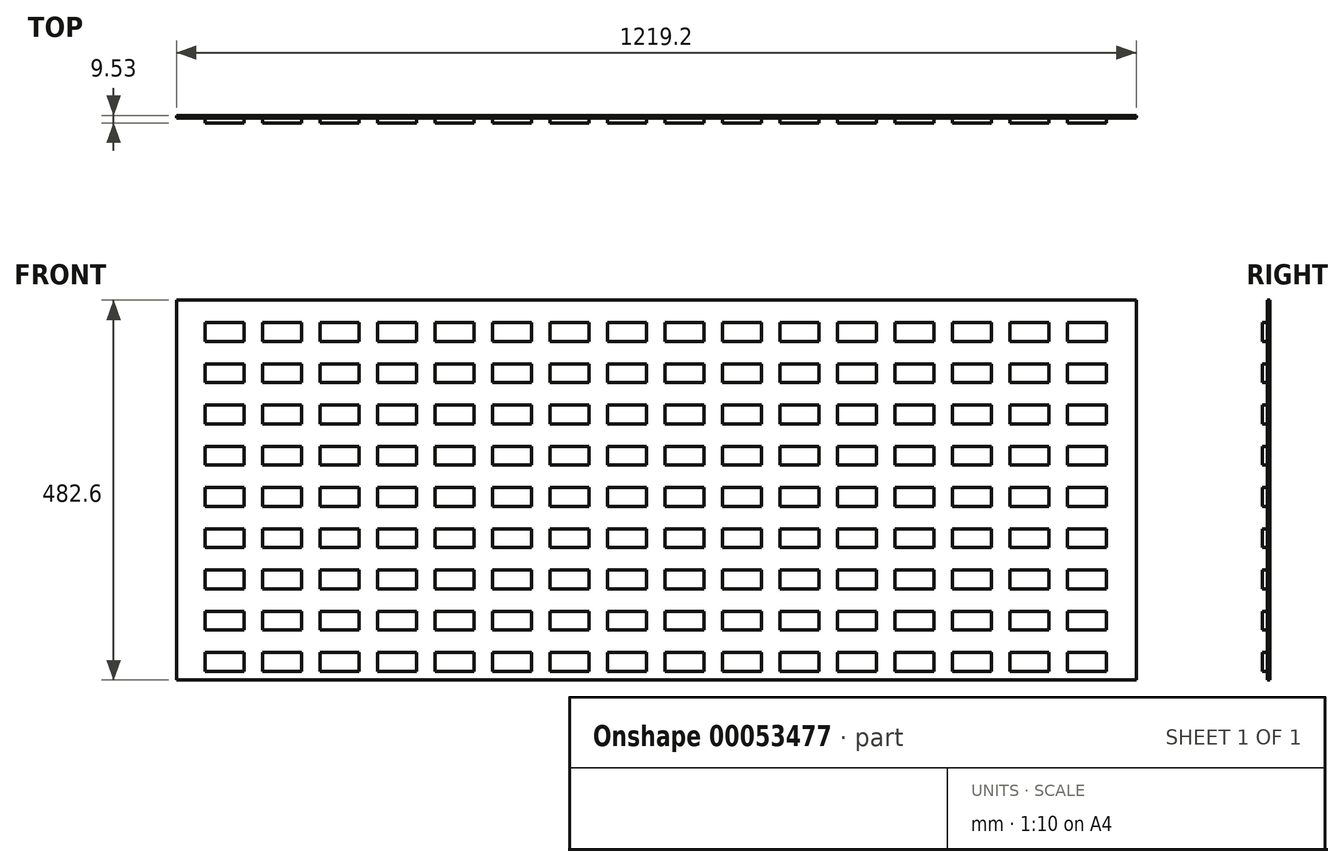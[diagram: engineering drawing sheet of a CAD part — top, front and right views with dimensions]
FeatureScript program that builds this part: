
annotation { "Feature Type Name" : "Feature", "Feature Type Description" : "" }
export const myFeature = defineFeature(function(context is Context, id is Id, definition is map)
    precondition{}
    {
        {
            var Q0;
            Q0=qCreatedBy(makeId("Front.planeOp"),FACE);
            var sketch = newSketch(context, id + "F0", { "sketchPlane" : qUnion([Q0])});
            skLineSegment(sketch, "E0.rect.bottom", {"start": v(-609.6, 241.3) * mm, "end": v(609.6, 241.3) * mm});
            skLineSegment(sketch, "E0.rect.top", {"start": v(-609.6, -241.3) * mm, "end": v(609.6, -241.3) * mm});
            skLineSegment(sketch, "E0.rect.left", {"start": v(-609.6, 241.3) * mm, "end": v(-609.6, -241.3) * mm});
            skLineSegment(sketch, "E0.rect.right", {"start": v(609.6, 241.3) * mm, "end": v(609.6, -241.3) * mm});
            skPoint(sketch, "E0.rect.middle", {"position": v(0, 0) * mm});
            skSolve(sketch);
        }
        {
            var Q0;
            Q0 = qSketchRegion(id + "F0", true);
            extrude(context, id + "F1", {"entities" : qUnion([Q0]), "depth" : 3.17 * mm});
        }
        {
            var Q0;
            Q0=makeQuery(id+"F1.opExtrude","CAP_FACE",FACE,{"disambiguationData":[OSD([sQuery(id+"F0.wireOp",EDGE,"E0.rect.bottom"),sQuery(id+"F0.wireOp",EDGE,"E0.rect.top"),sQuery(id+"F0.wireOp",EDGE,"E0.rect.left"),sQuery(id+"F0.wireOp",EDGE,"E0.rect.right")])],"isStart":false});
            var sketch = newSketch(context, id + "F2", { "sketchPlane" : qUnion([Q0])});
            skLineSegment(sketch, "E1", {"start": v(-609.6, 241.3) * mm, "end": v(-609.6, 212.72) * mm, "construction": true});
            skLineSegment(sketch, "E2", {"start": v(-609.6, 212.72) * mm, "end": v(-573.09, 212.72) * mm, "construction": true});
            skLineSegment(sketch, "E3", {"start": v(-573.09, 212.72) * mm, "end": v(-523.87, 212.72) * mm});
            skLineSegment(sketch, "E4", {"start": v(-523.87, 212.72) * mm, "end": v(-523.87, 188.91) * mm});
            skLineSegment(sketch, "E5", {"start": v(-523.87, 188.91) * mm, "end": v(-573.09, 188.91) * mm});
            skLineSegment(sketch, "E6", {"start": v(-573.09, 188.91) * mm, "end": v(-573.09, 212.72) * mm});
            skLineSegment(sketch, "E7", {"start": v(-548.48, 188.91) * mm, "end": v(-548.48, 160.34) * mm, "construction": true});
            skLineSegment(sketch, "E8.bottom", {"start": v(-573.09, 160.34) * mm, "end": v(-523.88, 160.34) * mm});
            skLineSegment(sketch, "E8.top", {"start": v(-573.09, 136.52) * mm, "end": v(-523.88, 136.52) * mm});
            skLineSegment(sketch, "E8.left", {"start": v(-573.09, 160.34) * mm, "end": v(-573.09, 136.52) * mm});
            skLineSegment(sketch, "E8.right", {"start": v(-523.88, 160.34) * mm, "end": v(-523.88, 136.52) * mm});
            skLineSegment(sketch, "E9", {"start": v(-523.87, 200.82) * mm, "end": v(-500.06, 200.82) * mm, "construction": true});
            skLineSegment(sketch, "E10", {"start": v(-500.06, 200.82) * mm, "end": v(-450.85, 200.82) * mm, "construction": true});
            skLineSegment(sketch, "E11", {"start": v(-450.85, 200.82) * mm, "end": v(-427.04, 200.82) * mm, "construction": true});
            skLineSegment(sketch, "E12", {"start": v(-427.04, 200.82) * mm, "end": v(-377.82, 200.82) * mm, "construction": true});
            skLineSegment(sketch, "E13", {"start": v(-377.82, 200.82) * mm, "end": v(-354.01, 200.82) * mm, "construction": true});
            skLineSegment(sketch, "E14", {"start": v(-354.01, 200.82) * mm, "end": v(-304.8, 200.82) * mm, "construction": true});
            skLineSegment(sketch, "E15", {"start": v(-304.8, 200.82) * mm, "end": v(-280.99, 200.82) * mm, "construction": true});
            skLineSegment(sketch, "E16", {"start": v(-280.99, 200.82) * mm, "end": v(-231.77, 200.82) * mm, "construction": true});
            skLineSegment(sketch, "E17", {"start": v(-231.77, 200.82) * mm, "end": v(-207.96, 200.82) * mm, "construction": true});
            skLineSegment(sketch, "E18", {"start": v(-207.96, 200.82) * mm, "end": v(-158.75, 200.82) * mm, "construction": true});
            skLineSegment(sketch, "E19", {"start": v(-158.75, 200.82) * mm, "end": v(-134.94, 200.82) * mm, "construction": true});
            skLineSegment(sketch, "E20", {"start": v(-134.94, 200.82) * mm, "end": v(-85.72, 200.82) * mm, "construction": true});
            skLineSegment(sketch, "E21", {"start": v(-85.72, 200.82) * mm, "end": v(-61.91, 200.82) * mm, "construction": true});
            skLineSegment(sketch, "E22", {"start": v(-61.91, 200.82) * mm, "end": v(-12.7, 200.82) * mm, "construction": true});
            skLineSegment(sketch, "E23", {"start": v(-12.7, 200.82) * mm, "end": v(11.11, 200.82) * mm, "construction": true});
            skLineSegment(sketch, "E24", {"start": v(11.11, 200.82) * mm, "end": v(60.33, 200.82) * mm, "construction": true});
            skLineSegment(sketch, "E25", {"start": v(60.33, 200.82) * mm, "end": v(84.14, 200.82) * mm, "construction": true});
            skLineSegment(sketch, "E26", {"start": v(84.14, 200.82) * mm, "end": v(133.35, 200.82) * mm, "construction": true});
            skLineSegment(sketch, "E27", {"start": v(133.35, 200.82) * mm, "end": v(157.16, 200.82) * mm, "construction": true});
            skLineSegment(sketch, "E28", {"start": v(157.16, 200.82) * mm, "end": v(206.38, 200.82) * mm, "construction": true});
            skLineSegment(sketch, "E29", {"start": v(206.38, 200.82) * mm, "end": v(230.19, 200.82) * mm, "construction": true});
            skLineSegment(sketch, "E30", {"start": v(230.19, 200.82) * mm, "end": v(279.4, 200.82) * mm, "construction": true});
            skLineSegment(sketch, "E31", {"start": v(279.4, 200.82) * mm, "end": v(303.21, 200.82) * mm, "construction": true});
            skLineSegment(sketch, "E32", {"start": v(303.21, 200.82) * mm, "end": v(352.43, 200.82) * mm, "construction": true});
            skLineSegment(sketch, "E33", {"start": v(352.43, 200.82) * mm, "end": v(376.24, 200.82) * mm, "construction": true});
            skLineSegment(sketch, "E34", {"start": v(376.24, 200.82) * mm, "end": v(425.45, 200.82) * mm, "construction": true});
            skLineSegment(sketch, "E35", {"start": v(425.45, 200.82) * mm, "end": v(449.26, 200.82) * mm, "construction": true});
            skLineSegment(sketch, "E36", {"start": v(449.26, 200.82) * mm, "end": v(498.48, 200.82) * mm, "construction": true});
            skLineSegment(sketch, "E37", {"start": v(498.48, 200.82) * mm, "end": v(522.29, 200.82) * mm, "construction": true});
            skLineSegment(sketch, "E38.rect.bottom", {"start": v(-450.85, 188.91) * mm, "end": v(-500.06, 188.91) * mm});
            skLineSegment(sketch, "E38.rect.top", {"start": v(-450.85, 212.73) * mm, "end": v(-500.06, 212.73) * mm});
            skLineSegment(sketch, "E38.rect.left", {"start": v(-450.85, 188.91) * mm, "end": v(-450.85, 212.73) * mm});
            skLineSegment(sketch, "E38.rect.right", {"start": v(-500.06, 188.91) * mm, "end": v(-500.06, 212.73) * mm});
            skPoint(sketch, "E38.rect.middle", {"position": v(-475.46, 200.82) * mm});
            skLineSegment(sketch, "E39.rect.bottom", {"start": v(-427.04, 188.91) * mm, "end": v(-377.82, 188.91) * mm});
            skLineSegment(sketch, "E39.rect.top", {"start": v(-427.04, 212.72) * mm, "end": v(-377.82, 212.72) * mm});
            skLineSegment(sketch, "E39.rect.left", {"start": v(-427.04, 188.91) * mm, "end": v(-427.04, 212.72) * mm});
            skLineSegment(sketch, "E39.rect.right", {"start": v(-377.82, 188.91) * mm, "end": v(-377.82, 212.72) * mm});
            skPoint(sketch, "E39.rect.middle", {"position": v(-402.43, 200.82) * mm});
            skLineSegment(sketch, "E40.rect.bottom", {"start": v(-354.01, 188.91) * mm, "end": v(-304.8, 188.91) * mm});
            skLineSegment(sketch, "E40.rect.top", {"start": v(-354.01, 212.73) * mm, "end": v(-304.8, 212.73) * mm});
            skLineSegment(sketch, "E40.rect.left", {"start": v(-354.01, 188.91) * mm, "end": v(-354.01, 212.73) * mm});
            skLineSegment(sketch, "E40.rect.right", {"start": v(-304.8, 188.91) * mm, "end": v(-304.8, 212.73) * mm});
            skPoint(sketch, "E40.rect.middle", {"position": v(-329.4, 200.82) * mm});
            skPoint(sketch, "E40.rect.cornerSnap0", {"position": v(-402.43, 188.91) * mm});
            skLineSegment(sketch, "E41.rect.bottom", {"start": v(-280.99, 188.91) * mm, "end": v(-231.77, 188.91) * mm});
            skLineSegment(sketch, "E41.rect.top", {"start": v(-280.99, 212.72) * mm, "end": v(-231.77, 212.72) * mm});
            skLineSegment(sketch, "E41.rect.left", {"start": v(-280.99, 188.91) * mm, "end": v(-280.99, 212.72) * mm});
            skLineSegment(sketch, "E41.rect.right", {"start": v(-231.77, 188.91) * mm, "end": v(-231.77, 212.72) * mm});
            skPoint(sketch, "E41.rect.middle", {"position": v(-256.38, 200.82) * mm});
            skLineSegment(sketch, "E42.rect.bottom", {"start": v(-207.96, 188.91) * mm, "end": v(-158.75, 188.91) * mm});
            skLineSegment(sketch, "E42.rect.top", {"start": v(-207.96, 212.72) * mm, "end": v(-158.75, 212.72) * mm});
            skLineSegment(sketch, "E42.rect.left", {"start": v(-207.96, 188.91) * mm, "end": v(-207.96, 212.72) * mm});
            skLineSegment(sketch, "E42.rect.right", {"start": v(-158.75, 188.91) * mm, "end": v(-158.75, 212.72) * mm});
            skPoint(sketch, "E42.rect.middle", {"position": v(-183.36, 200.82) * mm});
            skLineSegment(sketch, "E43.rect.bottom", {"start": v(-134.94, 188.91) * mm, "end": v(-85.72, 188.91) * mm});
            skLineSegment(sketch, "E43.rect.top", {"start": v(-134.94, 212.73) * mm, "end": v(-85.72, 212.73) * mm});
            skLineSegment(sketch, "E43.rect.left", {"start": v(-134.94, 188.91) * mm, "end": v(-134.94, 212.73) * mm});
            skLineSegment(sketch, "E43.rect.right", {"start": v(-85.72, 188.91) * mm, "end": v(-85.72, 212.73) * mm});
            skPoint(sketch, "E43.rect.middle", {"position": v(-110.33, 200.82) * mm});
            skLineSegment(sketch, "E44.rect.bottom", {"start": v(-61.91, 188.91) * mm, "end": v(-12.7, 188.91) * mm});
            skLineSegment(sketch, "E44.rect.top", {"start": v(-61.91, 212.73) * mm, "end": v(-12.7, 212.73) * mm});
            skLineSegment(sketch, "E44.rect.left", {"start": v(-61.91, 188.91) * mm, "end": v(-61.91, 212.73) * mm});
            skLineSegment(sketch, "E44.rect.right", {"start": v(-12.7, 188.91) * mm, "end": v(-12.7, 212.73) * mm});
            skPoint(sketch, "E44.rect.middle", {"position": v(-37.3, 200.82) * mm});
            skLineSegment(sketch, "E45.rect.bottom", {"start": v(11.11, 188.91) * mm, "end": v(60.33, 188.91) * mm});
            skLineSegment(sketch, "E45.rect.top", {"start": v(11.11, 212.73) * mm, "end": v(60.33, 212.73) * mm});
            skLineSegment(sketch, "E45.rect.left", {"start": v(11.11, 188.91) * mm, "end": v(11.11, 212.73) * mm});
            skLineSegment(sketch, "E45.rect.right", {"start": v(60.33, 188.91) * mm, "end": v(60.33, 212.73) * mm});
            skPoint(sketch, "E45.rect.middle", {"position": v(35.72, 200.82) * mm});
            skLineSegment(sketch, "E46.rect.bottom", {"start": v(84.14, 188.91) * mm, "end": v(133.35, 188.91) * mm});
            skLineSegment(sketch, "E46.rect.top", {"start": v(84.14, 212.72) * mm, "end": v(133.35, 212.72) * mm});
            skLineSegment(sketch, "E46.rect.left", {"start": v(84.14, 188.91) * mm, "end": v(84.14, 212.72) * mm});
            skLineSegment(sketch, "E46.rect.right", {"start": v(133.35, 188.91) * mm, "end": v(133.35, 212.72) * mm});
            skPoint(sketch, "E46.rect.middle", {"position": v(108.74, 200.82) * mm});
            skLineSegment(sketch, "E47.rect.bottom", {"start": v(157.16, 188.91) * mm, "end": v(206.38, 188.91) * mm});
            skLineSegment(sketch, "E47.rect.top", {"start": v(157.16, 212.72) * mm, "end": v(206.38, 212.72) * mm});
            skLineSegment(sketch, "E47.rect.left", {"start": v(157.16, 188.91) * mm, "end": v(157.16, 212.72) * mm});
            skLineSegment(sketch, "E47.rect.right", {"start": v(206.38, 188.91) * mm, "end": v(206.38, 212.72) * mm});
            skPoint(sketch, "E47.rect.middle", {"position": v(181.77, 200.82) * mm});
            skLineSegment(sketch, "E48.rect.bottom", {"start": v(230.19, 188.91) * mm, "end": v(279.4, 188.91) * mm});
            skLineSegment(sketch, "E48.rect.top", {"start": v(230.19, 212.72) * mm, "end": v(279.4, 212.72) * mm});
            skLineSegment(sketch, "E48.rect.left", {"start": v(230.19, 188.91) * mm, "end": v(230.19, 212.72) * mm});
            skLineSegment(sketch, "E48.rect.right", {"start": v(279.4, 188.91) * mm, "end": v(279.4, 212.72) * mm});
            skPoint(sketch, "E48.rect.middle", {"position": v(254.8, 200.82) * mm});
            skLineSegment(sketch, "E49.rect.bottom", {"start": v(303.21, 188.91) * mm, "end": v(352.43, 188.91) * mm});
            skLineSegment(sketch, "E49.rect.top", {"start": v(303.21, 212.73) * mm, "end": v(352.43, 212.73) * mm});
            skLineSegment(sketch, "E49.rect.left", {"start": v(303.21, 188.91) * mm, "end": v(303.21, 212.73) * mm});
            skLineSegment(sketch, "E49.rect.right", {"start": v(352.43, 188.91) * mm, "end": v(352.43, 212.73) * mm});
            skPoint(sketch, "E49.rect.middle", {"position": v(327.82, 200.82) * mm});
            skLineSegment(sketch, "E50.rect.bottom", {"start": v(376.24, 188.91) * mm, "end": v(425.45, 188.91) * mm});
            skLineSegment(sketch, "E50.rect.top", {"start": v(376.24, 212.73) * mm, "end": v(425.45, 212.73) * mm});
            skLineSegment(sketch, "E50.rect.left", {"start": v(376.24, 188.91) * mm, "end": v(376.24, 212.73) * mm});
            skLineSegment(sketch, "E50.rect.right", {"start": v(425.45, 188.91) * mm, "end": v(425.45, 212.73) * mm});
            skPoint(sketch, "E50.rect.middle", {"position": v(400.84, 200.82) * mm});
            skLineSegment(sketch, "E51.rect.bottom", {"start": v(449.26, 188.91) * mm, "end": v(498.48, 188.91) * mm});
            skLineSegment(sketch, "E51.rect.top", {"start": v(449.26, 212.73) * mm, "end": v(498.48, 212.73) * mm});
            skLineSegment(sketch, "E51.rect.left", {"start": v(449.26, 188.91) * mm, "end": v(449.26, 212.73) * mm});
            skLineSegment(sketch, "E51.rect.right", {"start": v(498.48, 188.91) * mm, "end": v(498.48, 212.73) * mm});
            skPoint(sketch, "E51.rect.middle", {"position": v(473.87, 200.82) * mm});
            skLineSegment(sketch, "E52", {"start": v(-523.88, 148.43) * mm, "end": v(-500.06, 148.43) * mm, "construction": true});
            skLineSegment(sketch, "E53", {"start": v(-500.06, 148.43) * mm, "end": v(-450.85, 148.43) * mm, "construction": true});
            skLineSegment(sketch, "E54", {"start": v(-450.85, 148.43) * mm, "end": v(-427.04, 148.43) * mm, "construction": true});
            skLineSegment(sketch, "E55", {"start": v(-427.04, 148.43) * mm, "end": v(-377.82, 148.43) * mm, "construction": true});
            skLineSegment(sketch, "E56", {"start": v(-377.82, 148.43) * mm, "end": v(-354.01, 148.43) * mm, "construction": true});
            skLineSegment(sketch, "E57", {"start": v(-354.01, 148.43) * mm, "end": v(-304.8, 148.43) * mm, "construction": true});
            skLineSegment(sketch, "E58", {"start": v(-304.8, 148.43) * mm, "end": v(-280.99, 148.43) * mm, "construction": true});
            skLineSegment(sketch, "E59", {"start": v(-280.99, 148.43) * mm, "end": v(-231.77, 148.43) * mm, "construction": true});
            skLineSegment(sketch, "E60", {"start": v(-231.77, 148.43) * mm, "end": v(-207.96, 148.43) * mm, "construction": true});
            skLineSegment(sketch, "E61", {"start": v(-207.96, 148.43) * mm, "end": v(-158.75, 148.43) * mm, "construction": true});
            skLineSegment(sketch, "E62.rect.bottom", {"start": v(-500.06, 160.34) * mm, "end": v(-450.85, 160.34) * mm});
            skLineSegment(sketch, "E62.rect.top", {"start": v(-500.06, 136.52) * mm, "end": v(-450.85, 136.52) * mm});
            skLineSegment(sketch, "E62.rect.left", {"start": v(-500.06, 160.34) * mm, "end": v(-500.06, 136.52) * mm});
            skLineSegment(sketch, "E62.rect.right", {"start": v(-450.85, 160.34) * mm, "end": v(-450.85, 136.52) * mm});
            skPoint(sketch, "E62.rect.middle", {"position": v(-475.46, 148.43) * mm});
            skLineSegment(sketch, "E63.rect.bottom", {"start": v(-427.04, 160.34) * mm, "end": v(-377.82, 160.34) * mm});
            skLineSegment(sketch, "E63.rect.top", {"start": v(-427.04, 136.53) * mm, "end": v(-377.82, 136.53) * mm});
            skLineSegment(sketch, "E63.rect.left", {"start": v(-427.04, 160.34) * mm, "end": v(-427.04, 136.53) * mm});
            skLineSegment(sketch, "E63.rect.right", {"start": v(-377.82, 160.34) * mm, "end": v(-377.82, 136.53) * mm});
            skPoint(sketch, "E63.rect.middle", {"position": v(-402.43, 148.43) * mm});
            skLineSegment(sketch, "E64.rect.bottom", {"start": v(-354.01, 160.34) * mm, "end": v(-304.8, 160.34) * mm});
            skLineSegment(sketch, "E64.rect.top", {"start": v(-354.01, 136.53) * mm, "end": v(-304.8, 136.53) * mm});
            skLineSegment(sketch, "E64.rect.left", {"start": v(-354.01, 160.34) * mm, "end": v(-354.01, 136.53) * mm});
            skLineSegment(sketch, "E64.rect.right", {"start": v(-304.8, 160.34) * mm, "end": v(-304.8, 136.53) * mm});
            skPoint(sketch, "E64.rect.middle", {"position": v(-329.4, 148.43) * mm});
            skLineSegment(sketch, "E65.rect.bottom", {"start": v(-280.99, 160.34) * mm, "end": v(-231.77, 160.34) * mm});
            skLineSegment(sketch, "E65.rect.top", {"start": v(-280.99, 136.52) * mm, "end": v(-231.77, 136.52) * mm});
            skLineSegment(sketch, "E65.rect.left", {"start": v(-280.99, 160.34) * mm, "end": v(-280.99, 136.52) * mm});
            skLineSegment(sketch, "E65.rect.right", {"start": v(-231.77, 160.34) * mm, "end": v(-231.77, 136.52) * mm});
            skPoint(sketch, "E65.rect.middle", {"position": v(-256.38, 148.43) * mm});
            skLineSegment(sketch, "E66.rect.bottom", {"start": v(-207.96, 160.34) * mm, "end": v(-158.75, 160.34) * mm});
            skLineSegment(sketch, "E66.rect.top", {"start": v(-207.96, 136.52) * mm, "end": v(-158.75, 136.52) * mm});
            skLineSegment(sketch, "E66.rect.left", {"start": v(-207.96, 160.34) * mm, "end": v(-207.96, 136.52) * mm});
            skLineSegment(sketch, "E66.rect.right", {"start": v(-158.75, 160.34) * mm, "end": v(-158.75, 136.52) * mm});
            skPoint(sketch, "E66.rect.middle", {"position": v(-183.36, 148.43) * mm});
            skLineSegment(sketch, "E67", {"start": v(-158.75, 148.43) * mm, "end": v(-134.94, 148.43) * mm, "construction": true});
            skLineSegment(sketch, "E68", {"start": v(-134.94, 148.43) * mm, "end": v(-85.72, 148.43) * mm, "construction": true});
            skLineSegment(sketch, "E69", {"start": v(-85.72, 148.43) * mm, "end": v(-61.91, 148.43) * mm, "construction": true});
            skLineSegment(sketch, "E70", {"start": v(-61.91, 148.43) * mm, "end": v(-12.7, 148.43) * mm, "construction": true});
            skLineSegment(sketch, "E71", {"start": v(-12.7, 148.43) * mm, "end": v(11.11, 148.43) * mm, "construction": true});
            skLineSegment(sketch, "E72", {"start": v(11.11, 148.43) * mm, "end": v(60.33, 148.43) * mm, "construction": true});
            skLineSegment(sketch, "E73", {"start": v(60.33, 148.43) * mm, "end": v(84.14, 148.43) * mm, "construction": true});
            skLineSegment(sketch, "E74", {"start": v(84.14, 148.43) * mm, "end": v(133.35, 148.43) * mm, "construction": true});
            skLineSegment(sketch, "E75", {"start": v(133.35, 148.43) * mm, "end": v(157.16, 148.43) * mm, "construction": true});
            skLineSegment(sketch, "E76", {"start": v(157.16, 148.43) * mm, "end": v(206.38, 148.43) * mm, "construction": true});
            skLineSegment(sketch, "E77.rect.bottom", {"start": v(-134.94, 160.34) * mm, "end": v(-85.72, 160.34) * mm});
            skLineSegment(sketch, "E77.rect.top", {"start": v(-134.94, 136.52) * mm, "end": v(-85.72, 136.52) * mm});
            skLineSegment(sketch, "E77.rect.left", {"start": v(-134.94, 160.34) * mm, "end": v(-134.94, 136.52) * mm});
            skLineSegment(sketch, "E77.rect.right", {"start": v(-85.72, 160.34) * mm, "end": v(-85.72, 136.52) * mm});
            skPoint(sketch, "E77.rect.middle", {"position": v(-110.33, 148.43) * mm});
            skLineSegment(sketch, "E78.rect.bottom", {"start": v(-61.91, 160.34) * mm, "end": v(-12.7, 160.34) * mm});
            skLineSegment(sketch, "E78.rect.top", {"start": v(-61.91, 136.52) * mm, "end": v(-12.7, 136.52) * mm});
            skLineSegment(sketch, "E78.rect.left", {"start": v(-61.91, 160.34) * mm, "end": v(-61.91, 136.52) * mm});
            skLineSegment(sketch, "E78.rect.right", {"start": v(-12.7, 160.34) * mm, "end": v(-12.7, 136.52) * mm});
            skPoint(sketch, "E78.rect.middle", {"position": v(-37.3, 148.43) * mm});
            skLineSegment(sketch, "E79.rect.bottom", {"start": v(11.11, 160.34) * mm, "end": v(60.33, 160.34) * mm});
            skLineSegment(sketch, "E79.rect.top", {"start": v(11.11, 136.52) * mm, "end": v(60.33, 136.52) * mm});
            skLineSegment(sketch, "E79.rect.left", {"start": v(11.11, 160.34) * mm, "end": v(11.11, 136.52) * mm});
            skLineSegment(sketch, "E79.rect.right", {"start": v(60.33, 160.34) * mm, "end": v(60.33, 136.52) * mm});
            skPoint(sketch, "E79.rect.middle", {"position": v(35.72, 148.43) * mm});
            skLineSegment(sketch, "E80.rect.bottom", {"start": v(84.14, 160.34) * mm, "end": v(133.35, 160.34) * mm});
            skLineSegment(sketch, "E80.rect.top", {"start": v(84.14, 136.52) * mm, "end": v(133.35, 136.52) * mm});
            skLineSegment(sketch, "E80.rect.left", {"start": v(84.14, 160.34) * mm, "end": v(84.14, 136.52) * mm});
            skLineSegment(sketch, "E80.rect.right", {"start": v(133.35, 160.34) * mm, "end": v(133.35, 136.52) * mm});
            skPoint(sketch, "E80.rect.middle", {"position": v(108.74, 148.43) * mm});
            skLineSegment(sketch, "E81.rect.bottom", {"start": v(157.16, 160.34) * mm, "end": v(206.38, 160.34) * mm});
            skLineSegment(sketch, "E81.rect.top", {"start": v(157.16, 136.52) * mm, "end": v(206.38, 136.52) * mm});
            skLineSegment(sketch, "E81.rect.left", {"start": v(157.16, 160.34) * mm, "end": v(157.16, 136.52) * mm});
            skLineSegment(sketch, "E81.rect.right", {"start": v(206.38, 160.34) * mm, "end": v(206.38, 136.52) * mm});
            skPoint(sketch, "E81.rect.middle", {"position": v(181.77, 148.43) * mm});
            skLineSegment(sketch, "E82", {"start": v(206.38, 148.43) * mm, "end": v(230.19, 148.43) * mm, "construction": true});
            skLineSegment(sketch, "E83", {"start": v(230.19, 148.43) * mm, "end": v(279.4, 148.43) * mm, "construction": true});
            skLineSegment(sketch, "E84", {"start": v(279.4, 148.43) * mm, "end": v(303.21, 148.43) * mm, "construction": true});
            skLineSegment(sketch, "E85", {"start": v(303.21, 148.43) * mm, "end": v(352.43, 148.43) * mm, "construction": true});
            skLineSegment(sketch, "E86", {"start": v(352.43, 148.43) * mm, "end": v(376.24, 148.43) * mm, "construction": true});
            skLineSegment(sketch, "E87", {"start": v(376.24, 148.43) * mm, "end": v(425.45, 148.43) * mm, "construction": true});
            skLineSegment(sketch, "E88", {"start": v(425.45, 148.43) * mm, "end": v(449.26, 148.43) * mm, "construction": true});
            skLineSegment(sketch, "E89", {"start": v(449.26, 148.43) * mm, "end": v(498.48, 148.43) * mm, "construction": true});
            skLineSegment(sketch, "E90.rect.bottom", {"start": v(230.19, 160.34) * mm, "end": v(279.4, 160.34) * mm});
            skLineSegment(sketch, "E90.rect.top", {"start": v(230.19, 136.52) * mm, "end": v(279.4, 136.52) * mm});
            skLineSegment(sketch, "E90.rect.left", {"start": v(230.19, 160.34) * mm, "end": v(230.19, 136.52) * mm});
            skLineSegment(sketch, "E90.rect.right", {"start": v(279.4, 160.34) * mm, "end": v(279.4, 136.52) * mm});
            skPoint(sketch, "E90.rect.middle", {"position": v(254.8, 148.43) * mm});
            skLineSegment(sketch, "E91.rect.bottom", {"start": v(303.21, 160.34) * mm, "end": v(352.43, 160.34) * mm});
            skLineSegment(sketch, "E91.rect.top", {"start": v(303.21, 136.52) * mm, "end": v(352.43, 136.52) * mm});
            skLineSegment(sketch, "E91.rect.left", {"start": v(303.21, 160.34) * mm, "end": v(303.21, 136.52) * mm});
            skLineSegment(sketch, "E91.rect.right", {"start": v(352.43, 160.34) * mm, "end": v(352.43, 136.52) * mm});
            skPoint(sketch, "E91.rect.middle", {"position": v(327.82, 148.43) * mm});
            skLineSegment(sketch, "E92.rect.bottom", {"start": v(376.24, 160.34) * mm, "end": v(425.45, 160.34) * mm});
            skLineSegment(sketch, "E92.rect.top", {"start": v(376.24, 136.52) * mm, "end": v(425.45, 136.52) * mm});
            skLineSegment(sketch, "E92.rect.left", {"start": v(376.24, 160.34) * mm, "end": v(376.24, 136.52) * mm});
            skLineSegment(sketch, "E92.rect.right", {"start": v(425.45, 160.34) * mm, "end": v(425.45, 136.52) * mm});
            skPoint(sketch, "E92.rect.middle", {"position": v(400.84, 148.43) * mm});
            skLineSegment(sketch, "E93.rect.bottom", {"start": v(449.26, 160.34) * mm, "end": v(498.48, 160.34) * mm});
            skLineSegment(sketch, "E93.rect.top", {"start": v(449.26, 136.52) * mm, "end": v(498.48, 136.52) * mm});
            skLineSegment(sketch, "E93.rect.left", {"start": v(449.26, 160.34) * mm, "end": v(449.26, 136.52) * mm});
            skLineSegment(sketch, "E93.rect.right", {"start": v(498.48, 160.34) * mm, "end": v(498.48, 136.52) * mm});
            skPoint(sketch, "E93.rect.middle", {"position": v(473.87, 148.43) * mm});
            skLineSegment(sketch, "E94", {"start": v(522.29, 200.82) * mm, "end": v(571.5, 200.82) * mm, "construction": true});
            skLineSegment(sketch, "E95", {"start": v(571.5, 200.82) * mm, "end": v(608.01, 200.82) * mm, "construction": true});
            skLineSegment(sketch, "E96.rect.bottom", {"start": v(522.29, 212.73) * mm, "end": v(571.5, 212.73) * mm});
            skLineSegment(sketch, "E96.rect.top", {"start": v(522.29, 188.91) * mm, "end": v(571.5, 188.91) * mm});
            skLineSegment(sketch, "E96.rect.left", {"start": v(522.29, 212.73) * mm, "end": v(522.29, 188.91) * mm});
            skLineSegment(sketch, "E96.rect.right", {"start": v(571.5, 212.73) * mm, "end": v(571.5, 188.91) * mm});
            skPoint(sketch, "E96.rect.middle", {"position": v(546.9, 200.82) * mm});
            skLineSegment(sketch, "E97", {"start": v(498.48, 148.43) * mm, "end": v(522.29, 148.43) * mm, "construction": true});
            skLineSegment(sketch, "E98", {"start": v(522.29, 148.43) * mm, "end": v(571.5, 148.43) * mm, "construction": true});
            skLineSegment(sketch, "E99.rect.bottom", {"start": v(522.29, 160.34) * mm, "end": v(571.5, 160.34) * mm});
            skLineSegment(sketch, "E99.rect.top", {"start": v(522.29, 136.52) * mm, "end": v(571.5, 136.52) * mm});
            skLineSegment(sketch, "E99.rect.left", {"start": v(522.29, 160.34) * mm, "end": v(522.29, 136.52) * mm});
            skLineSegment(sketch, "E99.rect.right", {"start": v(571.5, 160.34) * mm, "end": v(571.5, 136.52) * mm});
            skPoint(sketch, "E99.rect.middle", {"position": v(546.9, 148.43) * mm});
            skSolve(sketch);
        }
        {
            var Q0;
            Q0 = qSketchRegion(id + "F2", true);
            extrude(context, id + "F3", {"entities" : qUnion([Q0]), "operationType" : NewBodyOperationType.ADD, "depth" : 6.35 * mm});
        }
        {
            var Q0;
            Q0=makeQuery(id+"F1.opExtrude","CAP_FACE",FACE,{"disambiguationData":[OSD([sQuery(id+"F0.wireOp",EDGE,"E0.rect.bottom"),sQuery(id+"F0.wireOp",EDGE,"E0.rect.top"),sQuery(id+"F0.wireOp",EDGE,"E0.rect.left"),sQuery(id+"F0.wireOp",EDGE,"E0.rect.right")])],"isStart":false});
            var sketch = newSketch(context, id + "F4", { "sketchPlane" : qUnion([Q0])});
            skLineSegment(sketch, "E100", {"start": v(-548.48, 136.52) * mm, "end": v(-548.48, 107.95) * mm, "construction": true});
            skLineSegment(sketch, "E101", {"start": v(-548.48, 107.95) * mm, "end": v(-548.48, 84.14) * mm, "construction": true});
            skLineSegment(sketch, "E102", {"start": v(-548.48, 84.14) * mm, "end": v(-548.48, 55.56) * mm, "construction": true});
            skLineSegment(sketch, "E103", {"start": v(-548.48, 55.56) * mm, "end": v(-548.48, 31.75) * mm, "construction": true});
            skLineSegment(sketch, "E104.rect.bottom", {"start": v(-573.09, 107.95) * mm, "end": v(-523.88, 107.95) * mm});
            skLineSegment(sketch, "E104.rect.top", {"start": v(-573.09, 84.14) * mm, "end": v(-523.88, 84.14) * mm});
            skLineSegment(sketch, "E104.rect.left", {"start": v(-573.09, 107.95) * mm, "end": v(-573.09, 84.14) * mm});
            skLineSegment(sketch, "E104.rect.right", {"start": v(-523.88, 107.95) * mm, "end": v(-523.88, 84.14) * mm});
            skPoint(sketch, "E104.rect.middle", {"position": v(-548.48, 96.04) * mm});
            skLineSegment(sketch, "E105.rect.bottom", {"start": v(-573.09, 55.56) * mm, "end": v(-523.88, 55.56) * mm});
            skLineSegment(sketch, "E105.rect.top", {"start": v(-573.09, 31.75) * mm, "end": v(-523.88, 31.75) * mm});
            skLineSegment(sketch, "E105.rect.left", {"start": v(-573.09, 55.56) * mm, "end": v(-573.09, 31.75) * mm});
            skLineSegment(sketch, "E105.rect.right", {"start": v(-523.88, 55.56) * mm, "end": v(-523.88, 31.75) * mm});
            skPoint(sketch, "E105.rect.middle", {"position": v(-548.48, 43.66) * mm});
            skLineSegment(sketch, "E106", {"start": v(-548.48, 31.75) * mm, "end": v(-548.48, 3.17) * mm, "construction": true});
            skLineSegment(sketch, "E107", {"start": v(-548.48, 3.17) * mm, "end": v(-548.48, -20.64) * mm, "construction": true});
            skLineSegment(sketch, "E108.rect.bottom", {"start": v(-573.09, 3.17) * mm, "end": v(-523.88, 3.17) * mm});
            skLineSegment(sketch, "E108.rect.top", {"start": v(-573.09, -20.64) * mm, "end": v(-523.88, -20.64) * mm});
            skLineSegment(sketch, "E108.rect.left", {"start": v(-573.09, 3.17) * mm, "end": v(-573.09, -20.64) * mm});
            skLineSegment(sketch, "E108.rect.right", {"start": v(-523.88, 3.17) * mm, "end": v(-523.88, -20.64) * mm});
            skPoint(sketch, "E108.rect.middle", {"position": v(-548.48, -8.73) * mm});
            skLineSegment(sketch, "E109", {"start": v(-523.88, 96.04) * mm, "end": v(-500.06, 96.04) * mm, "construction": true});
            skLineSegment(sketch, "E110", {"start": v(-500.06, 96.04) * mm, "end": v(-450.85, 96.04) * mm, "construction": true});
            skLineSegment(sketch, "E111", {"start": v(-450.85, 96.04) * mm, "end": v(-427.04, 96.04) * mm, "construction": true});
            skLineSegment(sketch, "E112", {"start": v(-427.04, 96.04) * mm, "end": v(-377.82, 96.04) * mm, "construction": true});
            skLineSegment(sketch, "E113", {"start": v(-377.82, 96.04) * mm, "end": v(-354.01, 96.04) * mm, "construction": true});
            skLineSegment(sketch, "E114", {"start": v(-354.01, 96.04) * mm, "end": v(-304.8, 96.04) * mm, "construction": true});
            skLineSegment(sketch, "E115", {"start": v(-304.8, 96.04) * mm, "end": v(-280.99, 96.04) * mm, "construction": true});
            skLineSegment(sketch, "E116", {"start": v(-280.99, 96.04) * mm, "end": v(-231.77, 96.04) * mm, "construction": true});
            skLineSegment(sketch, "E117", {"start": v(-231.77, 96.04) * mm, "end": v(-207.96, 96.04) * mm, "construction": true});
            skLineSegment(sketch, "E118", {"start": v(-207.96, 96.04) * mm, "end": v(-158.75, 96.04) * mm, "construction": true});
            skLineSegment(sketch, "E119", {"start": v(-158.75, 96.04) * mm, "end": v(-134.94, 96.04) * mm, "construction": true});
            skLineSegment(sketch, "E120", {"start": v(-523.88, 43.66) * mm, "end": v(-500.06, 43.66) * mm, "construction": true});
            skLineSegment(sketch, "E121", {"start": v(-500.06, 43.66) * mm, "end": v(-450.85, 43.66) * mm, "construction": true});
            skLineSegment(sketch, "E122", {"start": v(-450.85, 43.66) * mm, "end": v(-427.04, 43.66) * mm, "construction": true});
            skLineSegment(sketch, "E123", {"start": v(-427.04, 43.66) * mm, "end": v(-377.82, 43.66) * mm, "construction": true});
            skLineSegment(sketch, "E124", {"start": v(-377.82, 43.66) * mm, "end": v(-354.01, 43.66) * mm, "construction": true});
            skLineSegment(sketch, "E125", {"start": v(-354.01, 43.66) * mm, "end": v(-304.8, 43.66) * mm, "construction": true});
            skLineSegment(sketch, "E126", {"start": v(-304.8, 43.66) * mm, "end": v(-280.99, 43.66) * mm, "construction": true});
            skLineSegment(sketch, "E127", {"start": v(-280.99, 43.66) * mm, "end": v(-231.77, 43.66) * mm, "construction": true});
            skLineSegment(sketch, "E128", {"start": v(-231.77, 43.66) * mm, "end": v(-207.96, 43.66) * mm, "construction": true});
            skLineSegment(sketch, "E129", {"start": v(-207.96, 43.66) * mm, "end": v(-158.75, 43.66) * mm, "construction": true});
            skLineSegment(sketch, "E130", {"start": v(-158.75, 43.66) * mm, "end": v(-134.94, 43.66) * mm, "construction": true});
            skLineSegment(sketch, "E131", {"start": v(-523.88, -8.73) * mm, "end": v(-500.06, -8.73) * mm, "construction": true});
            skLineSegment(sketch, "E132", {"start": v(-500.06, -8.73) * mm, "end": v(-450.85, -8.73) * mm, "construction": true});
            skLineSegment(sketch, "E133", {"start": v(-450.85, -8.73) * mm, "end": v(-427.04, -8.73) * mm, "construction": true});
            skLineSegment(sketch, "E134", {"start": v(-427.04, -8.73) * mm, "end": v(-377.82, -8.73) * mm, "construction": true});
            skLineSegment(sketch, "E135", {"start": v(-377.82, -8.73) * mm, "end": v(-354.01, -8.73) * mm, "construction": true});
            skLineSegment(sketch, "E136", {"start": v(-354.01, -8.73) * mm, "end": v(-304.8, -8.73) * mm, "construction": true});
            skLineSegment(sketch, "E137", {"start": v(-304.8, -8.73) * mm, "end": v(-280.99, -8.73) * mm, "construction": true});
            skLineSegment(sketch, "E138", {"start": v(-280.99, -8.73) * mm, "end": v(-231.77, -8.73) * mm, "construction": true});
            skLineSegment(sketch, "E139", {"start": v(-231.77, -8.73) * mm, "end": v(-207.96, -8.73) * mm, "construction": true});
            skLineSegment(sketch, "E140", {"start": v(-207.96, -8.73) * mm, "end": v(-158.75, -8.73) * mm, "construction": true});
            skLineSegment(sketch, "E141", {"start": v(-158.75, -8.73) * mm, "end": v(-134.94, -8.73) * mm, "construction": true});
            skLineSegment(sketch, "E142.rect.bottom", {"start": v(-500.06, 107.95) * mm, "end": v(-450.85, 107.95) * mm});
            skLineSegment(sketch, "E142.rect.top", {"start": v(-500.06, 84.14) * mm, "end": v(-450.85, 84.14) * mm});
            skLineSegment(sketch, "E142.rect.left", {"start": v(-500.06, 107.95) * mm, "end": v(-500.06, 84.14) * mm});
            skLineSegment(sketch, "E142.rect.right", {"start": v(-450.85, 107.95) * mm, "end": v(-450.85, 84.14) * mm});
            skPoint(sketch, "E142.rect.middle", {"position": v(-475.46, 96.04) * mm});
            skLineSegment(sketch, "E143.rect.bottom", {"start": v(-427.04, 107.95) * mm, "end": v(-377.82, 107.95) * mm});
            skLineSegment(sketch, "E143.rect.top", {"start": v(-427.04, 84.14) * mm, "end": v(-377.82, 84.14) * mm});
            skLineSegment(sketch, "E143.rect.left", {"start": v(-427.04, 107.95) * mm, "end": v(-427.04, 84.14) * mm});
            skLineSegment(sketch, "E143.rect.right", {"start": v(-377.82, 107.95) * mm, "end": v(-377.82, 84.14) * mm});
            skPoint(sketch, "E143.rect.middle", {"position": v(-402.43, 96.04) * mm});
            skLineSegment(sketch, "E144.rect.bottom", {"start": v(-354.01, 107.95) * mm, "end": v(-304.8, 107.95) * mm});
            skLineSegment(sketch, "E144.rect.top", {"start": v(-354.01, 84.14) * mm, "end": v(-304.8, 84.14) * mm});
            skLineSegment(sketch, "E144.rect.left", {"start": v(-354.01, 107.95) * mm, "end": v(-354.01, 84.14) * mm});
            skLineSegment(sketch, "E144.rect.right", {"start": v(-304.8, 107.95) * mm, "end": v(-304.8, 84.14) * mm});
            skPoint(sketch, "E144.rect.middle", {"position": v(-329.4, 96.04) * mm});
            skLineSegment(sketch, "E145.rect.bottom", {"start": v(-280.99, 107.95) * mm, "end": v(-231.77, 107.95) * mm});
            skLineSegment(sketch, "E145.rect.top", {"start": v(-280.99, 84.14) * mm, "end": v(-231.77, 84.14) * mm});
            skLineSegment(sketch, "E145.rect.left", {"start": v(-280.99, 107.95) * mm, "end": v(-280.99, 84.14) * mm});
            skLineSegment(sketch, "E145.rect.right", {"start": v(-231.77, 107.95) * mm, "end": v(-231.77, 84.14) * mm});
            skPoint(sketch, "E145.rect.middle", {"position": v(-256.38, 96.04) * mm});
            skLineSegment(sketch, "E146.rect.bottom", {"start": v(-207.96, 107.95) * mm, "end": v(-158.75, 107.95) * mm});
            skLineSegment(sketch, "E146.rect.top", {"start": v(-207.96, 84.14) * mm, "end": v(-158.75, 84.14) * mm});
            skLineSegment(sketch, "E146.rect.left", {"start": v(-207.96, 107.95) * mm, "end": v(-207.96, 84.14) * mm});
            skLineSegment(sketch, "E146.rect.right", {"start": v(-158.75, 107.95) * mm, "end": v(-158.75, 84.14) * mm});
            skPoint(sketch, "E146.rect.middle", {"position": v(-183.36, 96.04) * mm});
            skLineSegment(sketch, "E147.rect.bottom", {"start": v(-500.06, 55.56) * mm, "end": v(-450.85, 55.56) * mm});
            skLineSegment(sketch, "E147.rect.top", {"start": v(-500.06, 31.75) * mm, "end": v(-450.85, 31.75) * mm});
            skLineSegment(sketch, "E147.rect.left", {"start": v(-500.06, 55.56) * mm, "end": v(-500.06, 31.75) * mm});
            skLineSegment(sketch, "E147.rect.right", {"start": v(-450.85, 55.56) * mm, "end": v(-450.85, 31.75) * mm});
            skPoint(sketch, "E147.rect.middle", {"position": v(-475.46, 43.66) * mm});
            skLineSegment(sketch, "E148.rect.bottom", {"start": v(-427.04, 55.56) * mm, "end": v(-377.82, 55.56) * mm});
            skLineSegment(sketch, "E148.rect.top", {"start": v(-427.04, 31.75) * mm, "end": v(-377.82, 31.75) * mm});
            skLineSegment(sketch, "E148.rect.left", {"start": v(-427.04, 55.56) * mm, "end": v(-427.04, 31.75) * mm});
            skLineSegment(sketch, "E148.rect.right", {"start": v(-377.82, 55.56) * mm, "end": v(-377.82, 31.75) * mm});
            skPoint(sketch, "E148.rect.middle", {"position": v(-402.43, 43.66) * mm});
            skLineSegment(sketch, "E149.rect.bottom", {"start": v(-354.01, 55.56) * mm, "end": v(-304.8, 55.56) * mm});
            skLineSegment(sketch, "E149.rect.top", {"start": v(-354.01, 31.75) * mm, "end": v(-304.8, 31.75) * mm});
            skLineSegment(sketch, "E149.rect.left", {"start": v(-354.01, 55.56) * mm, "end": v(-354.01, 31.75) * mm});
            skLineSegment(sketch, "E149.rect.right", {"start": v(-304.8, 55.56) * mm, "end": v(-304.8, 31.75) * mm});
            skPoint(sketch, "E149.rect.middle", {"position": v(-329.4, 43.66) * mm});
            skLineSegment(sketch, "E150.rect.bottom", {"start": v(-280.99, 55.56) * mm, "end": v(-231.77, 55.56) * mm});
            skLineSegment(sketch, "E150.rect.top", {"start": v(-280.99, 31.75) * mm, "end": v(-231.77, 31.75) * mm});
            skLineSegment(sketch, "E150.rect.left", {"start": v(-280.99, 55.56) * mm, "end": v(-280.99, 31.75) * mm});
            skLineSegment(sketch, "E150.rect.right", {"start": v(-231.77, 55.56) * mm, "end": v(-231.77, 31.75) * mm});
            skPoint(sketch, "E150.rect.middle", {"position": v(-256.38, 43.66) * mm});
            skLineSegment(sketch, "E151.rect.bottom", {"start": v(-207.96, 55.56) * mm, "end": v(-158.75, 55.56) * mm});
            skLineSegment(sketch, "E151.rect.top", {"start": v(-207.96, 31.75) * mm, "end": v(-158.75, 31.75) * mm});
            skLineSegment(sketch, "E151.rect.left", {"start": v(-207.96, 55.56) * mm, "end": v(-207.96, 31.75) * mm});
            skLineSegment(sketch, "E151.rect.right", {"start": v(-158.75, 55.56) * mm, "end": v(-158.75, 31.75) * mm});
            skPoint(sketch, "E151.rect.middle", {"position": v(-183.36, 43.66) * mm});
            skLineSegment(sketch, "E152.rect.bottom", {"start": v(-500.06, 3.17) * mm, "end": v(-450.85, 3.17) * mm});
            skLineSegment(sketch, "E152.rect.top", {"start": v(-500.06, -20.64) * mm, "end": v(-450.85, -20.64) * mm});
            skLineSegment(sketch, "E152.rect.left", {"start": v(-500.06, 3.17) * mm, "end": v(-500.06, -20.64) * mm});
            skLineSegment(sketch, "E152.rect.right", {"start": v(-450.85, 3.17) * mm, "end": v(-450.85, -20.64) * mm});
            skPoint(sketch, "E152.rect.middle", {"position": v(-475.46, -8.73) * mm});
            skLineSegment(sketch, "E153.rect.bottom", {"start": v(-427.04, 3.17) * mm, "end": v(-377.82, 3.17) * mm});
            skLineSegment(sketch, "E153.rect.top", {"start": v(-427.04, -20.64) * mm, "end": v(-377.82, -20.64) * mm});
            skLineSegment(sketch, "E153.rect.left", {"start": v(-427.04, 3.17) * mm, "end": v(-427.04, -20.64) * mm});
            skLineSegment(sketch, "E153.rect.right", {"start": v(-377.82, 3.17) * mm, "end": v(-377.82, -20.64) * mm});
            skPoint(sketch, "E153.rect.middle", {"position": v(-402.43, -8.73) * mm});
            skLineSegment(sketch, "E154.rect.bottom", {"start": v(-354.01, 3.17) * mm, "end": v(-304.8, 3.17) * mm});
            skLineSegment(sketch, "E154.rect.top", {"start": v(-354.01, -20.64) * mm, "end": v(-304.8, -20.64) * mm});
            skLineSegment(sketch, "E154.rect.left", {"start": v(-354.01, 3.17) * mm, "end": v(-354.01, -20.64) * mm});
            skLineSegment(sketch, "E154.rect.right", {"start": v(-304.8, 3.17) * mm, "end": v(-304.8, -20.64) * mm});
            skPoint(sketch, "E154.rect.middle", {"position": v(-329.4, -8.73) * mm});
            skLineSegment(sketch, "E155.rect.bottom", {"start": v(-280.99, 3.17) * mm, "end": v(-231.77, 3.17) * mm});
            skLineSegment(sketch, "E155.rect.top", {"start": v(-280.99, -20.64) * mm, "end": v(-231.77, -20.64) * mm});
            skLineSegment(sketch, "E155.rect.left", {"start": v(-280.99, 3.17) * mm, "end": v(-280.99, -20.64) * mm});
            skLineSegment(sketch, "E155.rect.right", {"start": v(-231.77, 3.17) * mm, "end": v(-231.77, -20.64) * mm});
            skPoint(sketch, "E155.rect.middle", {"position": v(-256.38, -8.73) * mm});
            skLineSegment(sketch, "E156.rect.bottom", {"start": v(-207.96, 3.17) * mm, "end": v(-158.75, 3.17) * mm});
            skLineSegment(sketch, "E156.rect.top", {"start": v(-207.96, -20.64) * mm, "end": v(-158.75, -20.64) * mm});
            skLineSegment(sketch, "E156.rect.left", {"start": v(-207.96, 3.17) * mm, "end": v(-207.96, -20.64) * mm});
            skLineSegment(sketch, "E156.rect.right", {"start": v(-158.75, 3.17) * mm, "end": v(-158.75, -20.64) * mm});
            skPoint(sketch, "E156.rect.middle", {"position": v(-183.36, -8.73) * mm});
            skLineSegment(sketch, "E157", {"start": v(-134.94, 96.04) * mm, "end": v(-85.72, 96.04) * mm, "construction": true});
            skLineSegment(sketch, "E158", {"start": v(-85.72, 96.04) * mm, "end": v(-61.91, 96.04) * mm, "construction": true});
            skLineSegment(sketch, "E159", {"start": v(-61.91, 96.04) * mm, "end": v(-12.7, 96.04) * mm, "construction": true});
            skLineSegment(sketch, "E160", {"start": v(-12.7, 96.04) * mm, "end": v(11.11, 96.04) * mm, "construction": true});
            skLineSegment(sketch, "E161", {"start": v(11.11, 96.04) * mm, "end": v(60.33, 96.04) * mm, "construction": true});
            skLineSegment(sketch, "E162", {"start": v(60.33, 96.04) * mm, "end": v(84.14, 96.04) * mm, "construction": true});
            skLineSegment(sketch, "E163", {"start": v(84.14, 96.04) * mm, "end": v(133.35, 96.04) * mm, "construction": true});
            skLineSegment(sketch, "E164", {"start": v(133.35, 96.04) * mm, "end": v(157.16, 96.04) * mm, "construction": true});
            skLineSegment(sketch, "E165", {"start": v(157.16, 96.04) * mm, "end": v(206.38, 96.04) * mm, "construction": true});
            skLineSegment(sketch, "E166", {"start": v(206.38, 96.04) * mm, "end": v(230.19, 96.04) * mm, "construction": true});
            skLineSegment(sketch, "E167", {"start": v(230.19, 96.04) * mm, "end": v(279.4, 96.04) * mm, "construction": true});
            skLineSegment(sketch, "E168", {"start": v(279.4, 96.04) * mm, "end": v(303.21, 96.04) * mm, "construction": true});
            skLineSegment(sketch, "E169", {"start": v(303.21, 96.04) * mm, "end": v(352.43, 96.04) * mm, "construction": true});
            skLineSegment(sketch, "E170", {"start": v(352.43, 96.04) * mm, "end": v(376.24, 96.04) * mm, "construction": true});
            skLineSegment(sketch, "E171", {"start": v(376.24, 96.04) * mm, "end": v(425.45, 96.04) * mm, "construction": true});
            skLineSegment(sketch, "E172", {"start": v(425.45, 96.04) * mm, "end": v(449.26, 96.04) * mm, "construction": true});
            skLineSegment(sketch, "E173", {"start": v(449.26, 96.04) * mm, "end": v(498.48, 96.04) * mm, "construction": true});
            skLineSegment(sketch, "E174", {"start": v(498.48, 96.04) * mm, "end": v(522.29, 96.04) * mm, "construction": true});
            skLineSegment(sketch, "E175", {"start": v(522.29, 96.04) * mm, "end": v(571.5, 96.04) * mm, "construction": true});
            skLineSegment(sketch, "E176", {"start": v(-134.94, 43.66) * mm, "end": v(-85.72, 43.66) * mm, "construction": true});
            skLineSegment(sketch, "E177", {"start": v(-85.72, 43.66) * mm, "end": v(-61.91, 43.66) * mm, "construction": true});
            skLineSegment(sketch, "E178", {"start": v(-61.91, 43.66) * mm, "end": v(-12.7, 43.66) * mm, "construction": true});
            skLineSegment(sketch, "E179", {"start": v(-12.7, 43.66) * mm, "end": v(11.11, 43.66) * mm, "construction": true});
            skLineSegment(sketch, "E180", {"start": v(11.11, 43.66) * mm, "end": v(60.33, 43.66) * mm, "construction": true});
            skLineSegment(sketch, "E181", {"start": v(60.33, 43.66) * mm, "end": v(84.14, 43.66) * mm, "construction": true});
            skLineSegment(sketch, "E182", {"start": v(84.14, 43.66) * mm, "end": v(133.35, 43.66) * mm, "construction": true});
            skLineSegment(sketch, "E183", {"start": v(133.35, 43.66) * mm, "end": v(157.16, 43.66) * mm, "construction": true});
            skLineSegment(sketch, "E184", {"start": v(157.16, 43.66) * mm, "end": v(206.38, 43.66) * mm, "construction": true});
            skLineSegment(sketch, "E185", {"start": v(206.38, 43.66) * mm, "end": v(230.19, 43.66) * mm, "construction": true});
            skLineSegment(sketch, "E186", {"start": v(230.19, 43.66) * mm, "end": v(279.4, 43.66) * mm, "construction": true});
            skLineSegment(sketch, "E187", {"start": v(279.4, 43.66) * mm, "end": v(303.21, 43.66) * mm, "construction": true});
            skLineSegment(sketch, "E188", {"start": v(303.21, 43.66) * mm, "end": v(352.43, 43.66) * mm, "construction": true});
            skLineSegment(sketch, "E189", {"start": v(352.43, 43.66) * mm, "end": v(376.24, 43.66) * mm, "construction": true});
            skLineSegment(sketch, "E190", {"start": v(376.24, 43.66) * mm, "end": v(425.45, 43.66) * mm, "construction": true});
            skLineSegment(sketch, "E191", {"start": v(425.45, 43.66) * mm, "end": v(449.26, 43.66) * mm, "construction": true});
            skLineSegment(sketch, "E192", {"start": v(449.26, 43.66) * mm, "end": v(498.48, 43.66) * mm, "construction": true});
            skLineSegment(sketch, "E193", {"start": v(498.48, 43.66) * mm, "end": v(522.29, 43.66) * mm, "construction": true});
            skLineSegment(sketch, "E194", {"start": v(522.29, 43.66) * mm, "end": v(571.5, 43.66) * mm, "construction": true});
            skLineSegment(sketch, "E195", {"start": v(-134.94, -8.73) * mm, "end": v(-85.72, -8.73) * mm, "construction": true});
            skLineSegment(sketch, "E196", {"start": v(-85.72, -8.73) * mm, "end": v(-61.91, -8.73) * mm, "construction": true});
            skLineSegment(sketch, "E197", {"start": v(-61.91, -8.73) * mm, "end": v(-12.7, -8.73) * mm, "construction": true});
            skLineSegment(sketch, "E198", {"start": v(-12.7, -8.73) * mm, "end": v(11.11, -8.73) * mm, "construction": true});
            skLineSegment(sketch, "E199", {"start": v(11.11, -8.73) * mm, "end": v(60.33, -8.73) * mm, "construction": true});
            skLineSegment(sketch, "E200", {"start": v(60.33, -8.73) * mm, "end": v(84.14, -8.73) * mm, "construction": true});
            skLineSegment(sketch, "E201", {"start": v(84.14, -8.73) * mm, "end": v(133.35, -8.73) * mm, "construction": true});
            skLineSegment(sketch, "E202", {"start": v(133.35, -8.73) * mm, "end": v(157.16, -8.73) * mm, "construction": true});
            skLineSegment(sketch, "E203", {"start": v(157.16, -8.73) * mm, "end": v(206.38, -8.73) * mm, "construction": true});
            skLineSegment(sketch, "E204", {"start": v(206.38, -8.73) * mm, "end": v(230.19, -8.73) * mm, "construction": true});
            skLineSegment(sketch, "E205", {"start": v(230.19, -8.73) * mm, "end": v(279.4, -8.73) * mm, "construction": true});
            skLineSegment(sketch, "E206", {"start": v(279.4, -8.73) * mm, "end": v(303.21, -8.73) * mm, "construction": true});
            skLineSegment(sketch, "E207", {"start": v(303.21, -8.73) * mm, "end": v(352.43, -8.73) * mm, "construction": true});
            skLineSegment(sketch, "E208", {"start": v(352.43, -8.73) * mm, "end": v(376.24, -8.73) * mm, "construction": true});
            skLineSegment(sketch, "E209", {"start": v(376.24, -8.73) * mm, "end": v(425.45, -8.73) * mm, "construction": true});
            skLineSegment(sketch, "E210", {"start": v(425.45, -8.73) * mm, "end": v(449.26, -8.73) * mm, "construction": true});
            skLineSegment(sketch, "E211", {"start": v(449.26, -8.73) * mm, "end": v(498.48, -8.73) * mm, "construction": true});
            skLineSegment(sketch, "E212", {"start": v(498.48, -8.73) * mm, "end": v(522.29, -8.73) * mm, "construction": true});
            skLineSegment(sketch, "E213", {"start": v(522.29, -8.73) * mm, "end": v(571.5, -8.73) * mm, "construction": true});
            skLineSegment(sketch, "E214.rect.bottom", {"start": v(-134.94, 107.95) * mm, "end": v(-85.72, 107.95) * mm});
            skLineSegment(sketch, "E214.rect.top", {"start": v(-134.94, 84.14) * mm, "end": v(-85.72, 84.14) * mm});
            skLineSegment(sketch, "E214.rect.left", {"start": v(-134.94, 107.95) * mm, "end": v(-134.94, 84.14) * mm});
            skLineSegment(sketch, "E214.rect.right", {"start": v(-85.72, 107.95) * mm, "end": v(-85.72, 84.14) * mm});
            skPoint(sketch, "E214.rect.middle", {"position": v(-110.33, 96.04) * mm});
            skLineSegment(sketch, "E215.rect.bottom", {"start": v(-134.94, 55.56) * mm, "end": v(-85.72, 55.56) * mm});
            skLineSegment(sketch, "E215.rect.top", {"start": v(-134.94, 31.75) * mm, "end": v(-85.72, 31.75) * mm});
            skLineSegment(sketch, "E215.rect.left", {"start": v(-134.94, 55.56) * mm, "end": v(-134.94, 31.75) * mm});
            skLineSegment(sketch, "E215.rect.right", {"start": v(-85.72, 55.56) * mm, "end": v(-85.72, 31.75) * mm});
            skPoint(sketch, "E215.rect.middle", {"position": v(-110.33, 43.66) * mm});
            skLineSegment(sketch, "E216.rect.bottom", {"start": v(-134.94, 3.17) * mm, "end": v(-85.72, 3.17) * mm});
            skLineSegment(sketch, "E216.rect.top", {"start": v(-134.94, -20.64) * mm, "end": v(-85.72, -20.64) * mm});
            skLineSegment(sketch, "E216.rect.left", {"start": v(-134.94, 3.17) * mm, "end": v(-134.94, -20.64) * mm});
            skLineSegment(sketch, "E216.rect.right", {"start": v(-85.72, 3.17) * mm, "end": v(-85.72, -20.64) * mm});
            skPoint(sketch, "E216.rect.middle", {"position": v(-110.33, -8.73) * mm});
            skLineSegment(sketch, "E217.rect.bottom", {"start": v(-61.91, 3.17) * mm, "end": v(-12.7, 3.17) * mm});
            skLineSegment(sketch, "E217.rect.top", {"start": v(-61.91, -20.64) * mm, "end": v(-12.7, -20.64) * mm});
            skLineSegment(sketch, "E217.rect.left", {"start": v(-61.91, 3.17) * mm, "end": v(-61.91, -20.64) * mm});
            skLineSegment(sketch, "E217.rect.right", {"start": v(-12.7, 3.17) * mm, "end": v(-12.7, -20.64) * mm});
            skPoint(sketch, "E217.rect.middle", {"position": v(-37.3, -8.73) * mm});
            skLineSegment(sketch, "E218.rect.bottom", {"start": v(-61.91, 55.56) * mm, "end": v(-12.7, 55.56) * mm});
            skLineSegment(sketch, "E218.rect.top", {"start": v(-61.91, 31.75) * mm, "end": v(-12.7, 31.75) * mm});
            skLineSegment(sketch, "E218.rect.left", {"start": v(-61.91, 55.56) * mm, "end": v(-61.91, 31.75) * mm});
            skLineSegment(sketch, "E218.rect.right", {"start": v(-12.7, 55.56) * mm, "end": v(-12.7, 31.75) * mm});
            skPoint(sketch, "E218.rect.middle", {"position": v(-37.3, 43.66) * mm});
            skLineSegment(sketch, "E219.rect.bottom", {"start": v(-61.91, 107.95) * mm, "end": v(-12.7, 107.95) * mm});
            skLineSegment(sketch, "E219.rect.top", {"start": v(-61.91, 84.14) * mm, "end": v(-12.7, 84.14) * mm});
            skLineSegment(sketch, "E219.rect.left", {"start": v(-61.91, 107.95) * mm, "end": v(-61.91, 84.14) * mm});
            skLineSegment(sketch, "E219.rect.right", {"start": v(-12.7, 107.95) * mm, "end": v(-12.7, 84.14) * mm});
            skPoint(sketch, "E219.rect.middle", {"position": v(-37.3, 96.04) * mm});
            skLineSegment(sketch, "E220.rect.bottom", {"start": v(11.11, 107.95) * mm, "end": v(60.33, 107.95) * mm});
            skLineSegment(sketch, "E220.rect.top", {"start": v(11.11, 84.14) * mm, "end": v(60.33, 84.14) * mm});
            skLineSegment(sketch, "E220.rect.left", {"start": v(11.11, 107.95) * mm, "end": v(11.11, 84.14) * mm});
            skLineSegment(sketch, "E220.rect.right", {"start": v(60.33, 107.95) * mm, "end": v(60.33, 84.14) * mm});
            skPoint(sketch, "E220.rect.middle", {"position": v(35.72, 96.04) * mm});
            skLineSegment(sketch, "E221.rect.bottom", {"start": v(11.11, 55.56) * mm, "end": v(60.33, 55.56) * mm});
            skLineSegment(sketch, "E221.rect.top", {"start": v(11.11, 31.75) * mm, "end": v(60.33, 31.75) * mm});
            skLineSegment(sketch, "E221.rect.left", {"start": v(11.11, 55.56) * mm, "end": v(11.11, 31.75) * mm});
            skLineSegment(sketch, "E221.rect.right", {"start": v(60.33, 55.56) * mm, "end": v(60.33, 31.75) * mm});
            skPoint(sketch, "E221.rect.middle", {"position": v(35.72, 43.66) * mm});
            skLineSegment(sketch, "E222.rect.bottom", {"start": v(11.11, 3.17) * mm, "end": v(60.33, 3.17) * mm});
            skLineSegment(sketch, "E222.rect.top", {"start": v(11.11, -20.64) * mm, "end": v(60.33, -20.64) * mm});
            skLineSegment(sketch, "E222.rect.left", {"start": v(11.11, 3.17) * mm, "end": v(11.11, -20.64) * mm});
            skLineSegment(sketch, "E222.rect.right", {"start": v(60.33, 3.17) * mm, "end": v(60.33, -20.64) * mm});
            skPoint(sketch, "E222.rect.middle", {"position": v(35.72, -8.73) * mm});
            skLineSegment(sketch, "E223.rect.bottom", {"start": v(84.14, 3.17) * mm, "end": v(133.35, 3.17) * mm});
            skLineSegment(sketch, "E223.rect.top", {"start": v(84.14, -20.64) * mm, "end": v(133.35, -20.64) * mm});
            skLineSegment(sketch, "E223.rect.left", {"start": v(84.14, 3.17) * mm, "end": v(84.14, -20.64) * mm});
            skLineSegment(sketch, "E223.rect.right", {"start": v(133.35, 3.17) * mm, "end": v(133.35, -20.64) * mm});
            skPoint(sketch, "E223.rect.middle", {"position": v(108.74, -8.73) * mm});
            skLineSegment(sketch, "E224.rect.bottom", {"start": v(84.14, 55.56) * mm, "end": v(133.35, 55.56) * mm});
            skLineSegment(sketch, "E224.rect.top", {"start": v(84.14, 31.75) * mm, "end": v(133.35, 31.75) * mm});
            skLineSegment(sketch, "E224.rect.left", {"start": v(84.14, 55.56) * mm, "end": v(84.14, 31.75) * mm});
            skLineSegment(sketch, "E224.rect.right", {"start": v(133.35, 55.56) * mm, "end": v(133.35, 31.75) * mm});
            skPoint(sketch, "E224.rect.middle", {"position": v(108.74, 43.66) * mm});
            skLineSegment(sketch, "E225.rect.bottom", {"start": v(84.14, 107.95) * mm, "end": v(133.35, 107.95) * mm});
            skLineSegment(sketch, "E225.rect.top", {"start": v(84.14, 84.14) * mm, "end": v(133.35, 84.14) * mm});
            skLineSegment(sketch, "E225.rect.left", {"start": v(84.14, 107.95) * mm, "end": v(84.14, 84.14) * mm});
            skLineSegment(sketch, "E225.rect.right", {"start": v(133.35, 107.95) * mm, "end": v(133.35, 84.14) * mm});
            skPoint(sketch, "E225.rect.middle", {"position": v(108.74, 96.04) * mm});
            skLineSegment(sketch, "E226.rect.bottom", {"start": v(157.16, 107.95) * mm, "end": v(206.38, 107.95) * mm});
            skLineSegment(sketch, "E226.rect.top", {"start": v(157.16, 84.14) * mm, "end": v(206.38, 84.14) * mm});
            skLineSegment(sketch, "E226.rect.left", {"start": v(157.16, 107.95) * mm, "end": v(157.16, 84.14) * mm});
            skLineSegment(sketch, "E226.rect.right", {"start": v(206.38, 107.95) * mm, "end": v(206.38, 84.14) * mm});
            skPoint(sketch, "E226.rect.middle", {"position": v(181.77, 96.04) * mm});
            skLineSegment(sketch, "E227.rect.bottom", {"start": v(157.16, 55.56) * mm, "end": v(206.38, 55.56) * mm});
            skLineSegment(sketch, "E227.rect.top", {"start": v(157.16, 31.75) * mm, "end": v(206.38, 31.75) * mm});
            skLineSegment(sketch, "E227.rect.left", {"start": v(157.16, 55.56) * mm, "end": v(157.16, 31.75) * mm});
            skLineSegment(sketch, "E227.rect.right", {"start": v(206.38, 55.56) * mm, "end": v(206.38, 31.75) * mm});
            skPoint(sketch, "E227.rect.middle", {"position": v(181.77, 43.66) * mm});
            skLineSegment(sketch, "E228.rect.bottom", {"start": v(157.16, 3.17) * mm, "end": v(206.38, 3.17) * mm});
            skLineSegment(sketch, "E228.rect.top", {"start": v(157.16, -20.64) * mm, "end": v(206.38, -20.64) * mm});
            skLineSegment(sketch, "E228.rect.left", {"start": v(157.16, 3.17) * mm, "end": v(157.16, -20.64) * mm});
            skLineSegment(sketch, "E228.rect.right", {"start": v(206.38, 3.17) * mm, "end": v(206.38, -20.64) * mm});
            skPoint(sketch, "E228.rect.middle", {"position": v(181.77, -8.73) * mm});
            skLineSegment(sketch, "E229.rect.bottom", {"start": v(230.19, 3.17) * mm, "end": v(279.4, 3.17) * mm});
            skLineSegment(sketch, "E229.rect.top", {"start": v(230.19, -20.64) * mm, "end": v(279.4, -20.64) * mm});
            skLineSegment(sketch, "E229.rect.left", {"start": v(230.19, 3.17) * mm, "end": v(230.19, -20.64) * mm});
            skLineSegment(sketch, "E229.rect.right", {"start": v(279.4, 3.17) * mm, "end": v(279.4, -20.64) * mm});
            skPoint(sketch, "E229.rect.middle", {"position": v(254.8, -8.73) * mm});
            skLineSegment(sketch, "E230.rect.bottom", {"start": v(230.19, 55.56) * mm, "end": v(279.4, 55.56) * mm});
            skLineSegment(sketch, "E230.rect.top", {"start": v(230.19, 31.75) * mm, "end": v(279.4, 31.75) * mm});
            skLineSegment(sketch, "E230.rect.left", {"start": v(230.19, 55.56) * mm, "end": v(230.19, 31.75) * mm});
            skLineSegment(sketch, "E230.rect.right", {"start": v(279.4, 55.56) * mm, "end": v(279.4, 31.75) * mm});
            skPoint(sketch, "E230.rect.middle", {"position": v(254.8, 43.66) * mm});
            skLineSegment(sketch, "E231.rect.bottom", {"start": v(230.19, 107.95) * mm, "end": v(279.4, 107.95) * mm});
            skLineSegment(sketch, "E231.rect.top", {"start": v(230.19, 84.14) * mm, "end": v(279.4, 84.14) * mm});
            skLineSegment(sketch, "E231.rect.left", {"start": v(230.19, 107.95) * mm, "end": v(230.19, 84.14) * mm});
            skLineSegment(sketch, "E231.rect.right", {"start": v(279.4, 107.95) * mm, "end": v(279.4, 84.14) * mm});
            skPoint(sketch, "E231.rect.middle", {"position": v(254.8, 96.04) * mm});
            skLineSegment(sketch, "E232.rect.bottom", {"start": v(303.21, 107.95) * mm, "end": v(352.43, 107.95) * mm});
            skLineSegment(sketch, "E232.rect.top", {"start": v(303.21, 84.14) * mm, "end": v(352.43, 84.14) * mm});
            skLineSegment(sketch, "E232.rect.left", {"start": v(303.21, 107.95) * mm, "end": v(303.21, 84.14) * mm});
            skLineSegment(sketch, "E232.rect.right", {"start": v(352.43, 107.95) * mm, "end": v(352.43, 84.14) * mm});
            skPoint(sketch, "E232.rect.middle", {"position": v(327.82, 96.04) * mm});
            skLineSegment(sketch, "E233.rect.bottom", {"start": v(303.21, 55.56) * mm, "end": v(352.43, 55.56) * mm});
            skLineSegment(sketch, "E233.rect.top", {"start": v(303.21, 31.75) * mm, "end": v(352.43, 31.75) * mm});
            skLineSegment(sketch, "E233.rect.left", {"start": v(303.21, 55.56) * mm, "end": v(303.21, 31.75) * mm});
            skLineSegment(sketch, "E233.rect.right", {"start": v(352.43, 55.56) * mm, "end": v(352.43, 31.75) * mm});
            skPoint(sketch, "E233.rect.middle", {"position": v(327.82, 43.66) * mm});
            skLineSegment(sketch, "E234.rect.bottom", {"start": v(303.21, 3.17) * mm, "end": v(352.43, 3.17) * mm});
            skLineSegment(sketch, "E234.rect.top", {"start": v(303.21, -20.64) * mm, "end": v(352.43, -20.64) * mm});
            skLineSegment(sketch, "E234.rect.left", {"start": v(303.21, 3.17) * mm, "end": v(303.21, -20.64) * mm});
            skLineSegment(sketch, "E234.rect.right", {"start": v(352.43, 3.17) * mm, "end": v(352.43, -20.64) * mm});
            skPoint(sketch, "E234.rect.middle", {"position": v(327.82, -8.73) * mm});
            skLineSegment(sketch, "E235.rect.bottom", {"start": v(376.24, 107.95) * mm, "end": v(425.45, 107.95) * mm});
            skLineSegment(sketch, "E235.rect.top", {"start": v(376.24, 84.14) * mm, "end": v(425.45, 84.14) * mm});
            skLineSegment(sketch, "E235.rect.left", {"start": v(376.24, 107.95) * mm, "end": v(376.24, 84.14) * mm});
            skLineSegment(sketch, "E235.rect.right", {"start": v(425.45, 107.95) * mm, "end": v(425.45, 84.14) * mm});
            skPoint(sketch, "E235.rect.middle", {"position": v(400.84, 96.04) * mm});
            skLineSegment(sketch, "E236.rect.bottom", {"start": v(376.24, 55.56) * mm, "end": v(425.45, 55.56) * mm});
            skLineSegment(sketch, "E236.rect.top", {"start": v(376.24, 31.75) * mm, "end": v(425.45, 31.75) * mm});
            skLineSegment(sketch, "E236.rect.left", {"start": v(376.24, 55.56) * mm, "end": v(376.24, 31.75) * mm});
            skLineSegment(sketch, "E236.rect.right", {"start": v(425.45, 55.56) * mm, "end": v(425.45, 31.75) * mm});
            skPoint(sketch, "E236.rect.middle", {"position": v(400.84, 43.66) * mm});
            skLineSegment(sketch, "E237.rect.bottom", {"start": v(376.24, 3.17) * mm, "end": v(425.45, 3.17) * mm});
            skLineSegment(sketch, "E237.rect.top", {"start": v(376.24, -20.64) * mm, "end": v(425.45, -20.64) * mm});
            skLineSegment(sketch, "E237.rect.left", {"start": v(376.24, 3.17) * mm, "end": v(376.24, -20.64) * mm});
            skLineSegment(sketch, "E237.rect.right", {"start": v(425.45, 3.17) * mm, "end": v(425.45, -20.64) * mm});
            skPoint(sketch, "E237.rect.middle", {"position": v(400.84, -8.73) * mm});
            skLineSegment(sketch, "E238.rect.bottom", {"start": v(449.26, 107.95) * mm, "end": v(498.48, 107.95) * mm});
            skLineSegment(sketch, "E238.rect.top", {"start": v(449.26, 84.14) * mm, "end": v(498.48, 84.14) * mm});
            skLineSegment(sketch, "E238.rect.left", {"start": v(449.26, 107.95) * mm, "end": v(449.26, 84.14) * mm});
            skLineSegment(sketch, "E238.rect.right", {"start": v(498.48, 107.95) * mm, "end": v(498.48, 84.14) * mm});
            skPoint(sketch, "E238.rect.middle", {"position": v(473.87, 96.04) * mm});
            skLineSegment(sketch, "E239.rect.bottom", {"start": v(449.26, 55.56) * mm, "end": v(498.48, 55.56) * mm});
            skLineSegment(sketch, "E239.rect.top", {"start": v(449.26, 31.75) * mm, "end": v(498.48, 31.75) * mm});
            skLineSegment(sketch, "E239.rect.left", {"start": v(449.26, 55.56) * mm, "end": v(449.26, 31.75) * mm});
            skLineSegment(sketch, "E239.rect.right", {"start": v(498.48, 55.56) * mm, "end": v(498.48, 31.75) * mm});
            skPoint(sketch, "E239.rect.middle", {"position": v(473.87, 43.66) * mm});
            skLineSegment(sketch, "E240.rect.bottom", {"start": v(449.26, 3.17) * mm, "end": v(498.48, 3.17) * mm});
            skLineSegment(sketch, "E240.rect.top", {"start": v(449.26, -20.64) * mm, "end": v(498.48, -20.64) * mm});
            skLineSegment(sketch, "E240.rect.left", {"start": v(449.26, 3.17) * mm, "end": v(449.26, -20.64) * mm});
            skLineSegment(sketch, "E240.rect.right", {"start": v(498.48, 3.17) * mm, "end": v(498.48, -20.64) * mm});
            skPoint(sketch, "E240.rect.middle", {"position": v(473.87, -8.73) * mm});
            skLineSegment(sketch, "E241.rect.bottom", {"start": v(522.29, 107.95) * mm, "end": v(571.5, 107.95) * mm});
            skLineSegment(sketch, "E241.rect.top", {"start": v(522.29, 84.14) * mm, "end": v(571.5, 84.14) * mm});
            skLineSegment(sketch, "E241.rect.left", {"start": v(522.29, 107.95) * mm, "end": v(522.29, 84.14) * mm});
            skLineSegment(sketch, "E241.rect.right", {"start": v(571.5, 107.95) * mm, "end": v(571.5, 84.14) * mm});
            skPoint(sketch, "E241.rect.middle", {"position": v(546.9, 96.04) * mm});
            skLineSegment(sketch, "E242.rect.bottom", {"start": v(522.29, 55.56) * mm, "end": v(571.5, 55.56) * mm});
            skLineSegment(sketch, "E242.rect.top", {"start": v(522.29, 31.75) * mm, "end": v(571.5, 31.75) * mm});
            skLineSegment(sketch, "E242.rect.left", {"start": v(522.29, 55.56) * mm, "end": v(522.29, 31.75) * mm});
            skLineSegment(sketch, "E242.rect.right", {"start": v(571.5, 55.56) * mm, "end": v(571.5, 31.75) * mm});
            skPoint(sketch, "E242.rect.middle", {"position": v(546.9, 43.66) * mm});
            skLineSegment(sketch, "E243.rect.bottom", {"start": v(522.29, 3.17) * mm, "end": v(571.5, 3.17) * mm});
            skLineSegment(sketch, "E243.rect.top", {"start": v(522.29, -20.64) * mm, "end": v(571.5, -20.64) * mm});
            skLineSegment(sketch, "E243.rect.left", {"start": v(522.29, 3.17) * mm, "end": v(522.29, -20.64) * mm});
            skLineSegment(sketch, "E243.rect.right", {"start": v(571.5, 3.17) * mm, "end": v(571.5, -20.64) * mm});
            skPoint(sketch, "E243.rect.middle", {"position": v(546.9, -8.73) * mm});
            skSolve(sketch);
        }
        {
            var Q0;
            Q0 = qSketchRegion(id + "F4", true);
            extrude(context, id + "F5", {"entities" : qUnion([Q0]), "operationType" : NewBodyOperationType.ADD, "depth" : 6.35 * mm});
        }
        {
            var Q0;
            Q0=makeQuery(id+"F1.opExtrude","CAP_FACE",FACE,{"disambiguationData":[OSD([sQuery(id+"F0.wireOp",EDGE,"E0.rect.bottom"),sQuery(id+"F0.wireOp",EDGE,"E0.rect.top"),sQuery(id+"F0.wireOp",EDGE,"E0.rect.left"),sQuery(id+"F0.wireOp",EDGE,"E0.rect.right")])],"isStart":false});
            var sketch = newSketch(context, id + "F6", { "sketchPlane" : qUnion([Q0])});
            skLineSegment(sketch, "E244", {"start": v(-548.48, -20.64) * mm, "end": v(-548.48, -49.21) * mm, "construction": true});
            skLineSegment(sketch, "E245", {"start": v(-548.48, -49.21) * mm, "end": v(-548.48, -73.03) * mm, "construction": true});
            skLineSegment(sketch, "E246", {"start": v(-548.48, -73.03) * mm, "end": v(-548.48, -101.6) * mm, "construction": true});
            skLineSegment(sketch, "E247", {"start": v(-548.48, -101.6) * mm, "end": v(-548.48, -125.41) * mm, "construction": true});
            skLineSegment(sketch, "E248", {"start": v(-548.48, -125.41) * mm, "end": v(-548.48, -153.99) * mm, "construction": true});
            skLineSegment(sketch, "E249", {"start": v(-548.48, -153.99) * mm, "end": v(-548.48, -177.8) * mm, "construction": true});
            skLineSegment(sketch, "E250", {"start": v(-548.48, -177.8) * mm, "end": v(-548.48, -206.38) * mm, "construction": true});
            skLineSegment(sketch, "E251", {"start": v(-548.48, -206.38) * mm, "end": v(-548.48, -230.19) * mm, "construction": true});
            skLineSegment(sketch, "E252.rect.bottom", {"start": v(-573.09, -49.21) * mm, "end": v(-523.88, -49.21) * mm});
            skLineSegment(sketch, "E252.rect.top", {"start": v(-573.09, -73.03) * mm, "end": v(-523.88, -73.03) * mm});
            skLineSegment(sketch, "E252.rect.left", {"start": v(-573.09, -49.21) * mm, "end": v(-573.09, -73.03) * mm});
            skLineSegment(sketch, "E252.rect.right", {"start": v(-523.88, -49.21) * mm, "end": v(-523.88, -73.03) * mm});
            skPoint(sketch, "E252.rect.middle", {"position": v(-548.48, -61.12) * mm});
            skLineSegment(sketch, "E253.rect.bottom", {"start": v(-573.09, -101.6) * mm, "end": v(-523.88, -101.6) * mm});
            skLineSegment(sketch, "E253.rect.top", {"start": v(-573.09, -125.41) * mm, "end": v(-523.88, -125.41) * mm});
            skLineSegment(sketch, "E253.rect.left", {"start": v(-573.09, -101.6) * mm, "end": v(-573.09, -125.41) * mm});
            skLineSegment(sketch, "E253.rect.right", {"start": v(-523.88, -101.6) * mm, "end": v(-523.88, -125.41) * mm});
            skPoint(sketch, "E253.rect.middle", {"position": v(-548.48, -113.5) * mm});
            skLineSegment(sketch, "E254.rect.bottom", {"start": v(-573.09, -153.99) * mm, "end": v(-523.88, -153.99) * mm});
            skLineSegment(sketch, "E254.rect.top", {"start": v(-573.09, -177.8) * mm, "end": v(-523.88, -177.8) * mm});
            skLineSegment(sketch, "E254.rect.left", {"start": v(-573.09, -153.99) * mm, "end": v(-573.09, -177.8) * mm});
            skLineSegment(sketch, "E254.rect.right", {"start": v(-523.88, -153.99) * mm, "end": v(-523.88, -177.8) * mm});
            skPoint(sketch, "E254.rect.middle", {"position": v(-548.48, -165.9) * mm});
            skLineSegment(sketch, "E255.rect.bottom", {"start": v(-573.09, -206.38) * mm, "end": v(-523.88, -206.38) * mm});
            skLineSegment(sketch, "E255.rect.top", {"start": v(-573.09, -230.19) * mm, "end": v(-523.88, -230.19) * mm});
            skLineSegment(sketch, "E255.rect.left", {"start": v(-573.09, -206.38) * mm, "end": v(-573.09, -230.19) * mm});
            skLineSegment(sketch, "E255.rect.right", {"start": v(-523.88, -206.38) * mm, "end": v(-523.88, -230.19) * mm});
            skPoint(sketch, "E255.rect.middle", {"position": v(-548.48, -218.28) * mm});
            skLineSegment(sketch, "E256", {"start": v(-523.88, -61.12) * mm, "end": v(-500.06, -61.12) * mm, "construction": true});
            skLineSegment(sketch, "E257", {"start": v(-500.06, -61.12) * mm, "end": v(-450.85, -61.12) * mm, "construction": true});
            skLineSegment(sketch, "E258", {"start": v(-450.85, -61.12) * mm, "end": v(-427.04, -61.12) * mm, "construction": true});
            skLineSegment(sketch, "E259", {"start": v(-427.04, -61.12) * mm, "end": v(-377.82, -61.12) * mm, "construction": true});
            skLineSegment(sketch, "E260", {"start": v(-377.82, -61.12) * mm, "end": v(-354.01, -61.12) * mm, "construction": true});
            skLineSegment(sketch, "E261", {"start": v(-354.01, -61.12) * mm, "end": v(-304.8, -61.12) * mm, "construction": true});
            skLineSegment(sketch, "E262", {"start": v(-304.8, -61.12) * mm, "end": v(-280.99, -61.12) * mm, "construction": true});
            skLineSegment(sketch, "E263", {"start": v(-280.99, -61.12) * mm, "end": v(-231.77, -61.12) * mm, "construction": true});
            skLineSegment(sketch, "E264", {"start": v(-231.77, -61.12) * mm, "end": v(-207.96, -61.12) * mm, "construction": true});
            skLineSegment(sketch, "E265", {"start": v(-207.96, -61.12) * mm, "end": v(-158.75, -61.12) * mm, "construction": true});
            skLineSegment(sketch, "E266", {"start": v(-158.75, -61.12) * mm, "end": v(-134.94, -61.12) * mm, "construction": true});
            skLineSegment(sketch, "E267", {"start": v(-134.94, -61.12) * mm, "end": v(-85.72, -61.12) * mm, "construction": true});
            skLineSegment(sketch, "E268", {"start": v(-85.72, -61.12) * mm, "end": v(-61.91, -61.12) * mm, "construction": true});
            skLineSegment(sketch, "E269", {"start": v(-61.91, -61.12) * mm, "end": v(-12.7, -61.12) * mm, "construction": true});
            skLineSegment(sketch, "E270", {"start": v(-12.7, -61.12) * mm, "end": v(11.11, -61.12) * mm, "construction": true});
            skLineSegment(sketch, "E271", {"start": v(11.11, -61.12) * mm, "end": v(60.33, -61.12) * mm, "construction": true});
            skLineSegment(sketch, "E272", {"start": v(60.33, -61.12) * mm, "end": v(84.14, -61.12) * mm, "construction": true});
            skLineSegment(sketch, "E273", {"start": v(-523.88, -113.5) * mm, "end": v(-500.06, -113.5) * mm, "construction": true});
            skLineSegment(sketch, "E274", {"start": v(-500.06, -113.5) * mm, "end": v(-450.85, -113.5) * mm, "construction": true});
            skLineSegment(sketch, "E275", {"start": v(-450.85, -113.5) * mm, "end": v(-427.04, -113.5) * mm, "construction": true});
            skLineSegment(sketch, "E276", {"start": v(-427.04, -113.5) * mm, "end": v(-377.82, -113.5) * mm, "construction": true});
            skLineSegment(sketch, "E277", {"start": v(-377.82, -113.5) * mm, "end": v(-354.01, -113.5) * mm, "construction": true});
            skLineSegment(sketch, "E278", {"start": v(-354.01, -113.5) * mm, "end": v(-304.8, -113.5) * mm, "construction": true});
            skLineSegment(sketch, "E279", {"start": v(-304.8, -113.5) * mm, "end": v(-280.99, -113.5) * mm, "construction": true});
            skLineSegment(sketch, "E280", {"start": v(-280.99, -113.5) * mm, "end": v(-231.77, -113.5) * mm, "construction": true});
            skLineSegment(sketch, "E281", {"start": v(-231.77, -113.5) * mm, "end": v(-207.96, -113.5) * mm, "construction": true});
            skLineSegment(sketch, "E282", {"start": v(-207.96, -113.5) * mm, "end": v(-158.75, -113.5) * mm, "construction": true});
            skLineSegment(sketch, "E283", {"start": v(-158.75, -113.5) * mm, "end": v(-134.94, -113.5) * mm, "construction": true});
            skLineSegment(sketch, "E284", {"start": v(-134.94, -113.5) * mm, "end": v(-85.72, -113.5) * mm, "construction": true});
            skLineSegment(sketch, "E285", {"start": v(-85.72, -113.5) * mm, "end": v(-61.91, -113.5) * mm, "construction": true});
            skLineSegment(sketch, "E286", {"start": v(-61.91, -113.5) * mm, "end": v(-12.7, -113.5) * mm, "construction": true});
            skLineSegment(sketch, "E287", {"start": v(-12.7, -113.5) * mm, "end": v(11.11, -113.5) * mm, "construction": true});
            skLineSegment(sketch, "E288", {"start": v(11.11, -113.5) * mm, "end": v(60.33, -113.5) * mm, "construction": true});
            skLineSegment(sketch, "E289", {"start": v(60.33, -113.5) * mm, "end": v(84.14, -113.5) * mm, "construction": true});
            skLineSegment(sketch, "E290", {"start": v(-523.88, -165.9) * mm, "end": v(-500.06, -165.9) * mm, "construction": true});
            skLineSegment(sketch, "E291", {"start": v(-500.06, -165.9) * mm, "end": v(-450.85, -165.9) * mm, "construction": true});
            skLineSegment(sketch, "E292", {"start": v(-450.85, -165.9) * mm, "end": v(-427.04, -165.9) * mm, "construction": true});
            skLineSegment(sketch, "E293", {"start": v(-427.04, -165.9) * mm, "end": v(-377.82, -165.9) * mm, "construction": true});
            skLineSegment(sketch, "E294", {"start": v(-377.82, -165.9) * mm, "end": v(-354.01, -165.9) * mm, "construction": true});
            skLineSegment(sketch, "E295", {"start": v(-354.01, -165.9) * mm, "end": v(-304.8, -165.9) * mm, "construction": true});
            skLineSegment(sketch, "E296", {"start": v(-304.8, -165.9) * mm, "end": v(-280.99, -165.9) * mm, "construction": true});
            skLineSegment(sketch, "E297", {"start": v(-280.99, -165.9) * mm, "end": v(-231.77, -165.9) * mm, "construction": true});
            skLineSegment(sketch, "E298", {"start": v(-231.77, -165.9) * mm, "end": v(-207.96, -165.9) * mm, "construction": true});
            skLineSegment(sketch, "E299", {"start": v(-207.96, -165.9) * mm, "end": v(-158.75, -165.9) * mm, "construction": true});
            skLineSegment(sketch, "E300", {"start": v(-158.75, -165.9) * mm, "end": v(-134.94, -165.9) * mm, "construction": true});
            skLineSegment(sketch, "E301", {"start": v(-134.94, -165.9) * mm, "end": v(-85.72, -165.9) * mm, "construction": true});
            skLineSegment(sketch, "E302", {"start": v(-85.72, -165.9) * mm, "end": v(-61.91, -165.9) * mm, "construction": true});
            skLineSegment(sketch, "E303", {"start": v(-61.91, -165.9) * mm, "end": v(-12.7, -165.9) * mm, "construction": true});
            skLineSegment(sketch, "E304", {"start": v(-12.7, -165.9) * mm, "end": v(11.11, -165.9) * mm, "construction": true});
            skLineSegment(sketch, "E305", {"start": v(11.11, -165.9) * mm, "end": v(60.33, -165.9) * mm, "construction": true});
            skLineSegment(sketch, "E306", {"start": v(60.33, -165.9) * mm, "end": v(84.14, -165.9) * mm, "construction": true});
            skLineSegment(sketch, "E307", {"start": v(-523.88, -218.28) * mm, "end": v(-500.06, -218.28) * mm, "construction": true});
            skLineSegment(sketch, "E308", {"start": v(-500.06, -218.28) * mm, "end": v(-450.85, -218.28) * mm, "construction": true});
            skLineSegment(sketch, "E309", {"start": v(-450.85, -218.28) * mm, "end": v(-427.04, -218.28) * mm, "construction": true});
            skLineSegment(sketch, "E310", {"start": v(-427.04, -218.28) * mm, "end": v(-377.82, -218.28) * mm, "construction": true});
            skLineSegment(sketch, "E311", {"start": v(-377.82, -218.28) * mm, "end": v(-354.01, -218.28) * mm, "construction": true});
            skLineSegment(sketch, "E312", {"start": v(-354.01, -218.28) * mm, "end": v(-304.8, -218.28) * mm, "construction": true});
            skLineSegment(sketch, "E313", {"start": v(-304.8, -218.28) * mm, "end": v(-280.99, -218.28) * mm, "construction": true});
            skLineSegment(sketch, "E314", {"start": v(-280.99, -218.28) * mm, "end": v(-231.77, -218.28) * mm, "construction": true});
            skLineSegment(sketch, "E315", {"start": v(-231.77, -218.28) * mm, "end": v(-207.96, -218.28) * mm, "construction": true});
            skLineSegment(sketch, "E316", {"start": v(-207.96, -218.28) * mm, "end": v(-158.75, -218.28) * mm, "construction": true});
            skLineSegment(sketch, "E317", {"start": v(-158.75, -218.28) * mm, "end": v(-134.94, -218.28) * mm, "construction": true});
            skLineSegment(sketch, "E318", {"start": v(-134.94, -218.28) * mm, "end": v(-85.72, -218.28) * mm, "construction": true});
            skLineSegment(sketch, "E319", {"start": v(-85.72, -218.28) * mm, "end": v(-61.91, -218.28) * mm, "construction": true});
            skLineSegment(sketch, "E320", {"start": v(-61.91, -218.28) * mm, "end": v(-12.7, -218.28) * mm, "construction": true});
            skLineSegment(sketch, "E321", {"start": v(-12.7, -218.28) * mm, "end": v(11.11, -218.28) * mm, "construction": true});
            skLineSegment(sketch, "E322", {"start": v(11.11, -218.28) * mm, "end": v(60.33, -218.28) * mm, "construction": true});
            skLineSegment(sketch, "E323", {"start": v(60.33, -218.28) * mm, "end": v(84.14, -218.28) * mm, "construction": true});
            skLineSegment(sketch, "E324.rect.bottom", {"start": v(-500.06, -49.21) * mm, "end": v(-450.85, -49.21) * mm});
            skLineSegment(sketch, "E324.rect.top", {"start": v(-500.06, -73.03) * mm, "end": v(-450.85, -73.03) * mm});
            skLineSegment(sketch, "E324.rect.left", {"start": v(-500.06, -49.21) * mm, "end": v(-500.06, -73.03) * mm});
            skLineSegment(sketch, "E324.rect.right", {"start": v(-450.85, -49.21) * mm, "end": v(-450.85, -73.03) * mm});
            skPoint(sketch, "E324.rect.middle", {"position": v(-475.46, -61.12) * mm});
            skLineSegment(sketch, "E325.rect.bottom", {"start": v(-427.04, -49.21) * mm, "end": v(-377.82, -49.21) * mm});
            skLineSegment(sketch, "E325.rect.top", {"start": v(-427.04, -73.03) * mm, "end": v(-377.82, -73.03) * mm});
            skLineSegment(sketch, "E325.rect.left", {"start": v(-427.04, -49.21) * mm, "end": v(-427.04, -73.03) * mm});
            skLineSegment(sketch, "E325.rect.right", {"start": v(-377.82, -49.21) * mm, "end": v(-377.82, -73.03) * mm});
            skPoint(sketch, "E325.rect.middle", {"position": v(-402.43, -61.12) * mm});
            skLineSegment(sketch, "E326.rect.bottom", {"start": v(-500.06, -101.6) * mm, "end": v(-450.85, -101.6) * mm});
            skLineSegment(sketch, "E326.rect.top", {"start": v(-500.06, -125.41) * mm, "end": v(-450.85, -125.41) * mm});
            skLineSegment(sketch, "E326.rect.left", {"start": v(-500.06, -101.6) * mm, "end": v(-500.06, -125.41) * mm});
            skLineSegment(sketch, "E326.rect.right", {"start": v(-450.85, -101.6) * mm, "end": v(-450.85, -125.41) * mm});
            skPoint(sketch, "E326.rect.middle", {"position": v(-475.46, -113.5) * mm});
            skLineSegment(sketch, "E327.rect.bottom", {"start": v(-500.06, -153.99) * mm, "end": v(-450.85, -153.99) * mm});
            skLineSegment(sketch, "E327.rect.top", {"start": v(-500.06, -177.8) * mm, "end": v(-450.85, -177.8) * mm});
            skLineSegment(sketch, "E327.rect.left", {"start": v(-500.06, -153.99) * mm, "end": v(-500.06, -177.8) * mm});
            skLineSegment(sketch, "E327.rect.right", {"start": v(-450.85, -153.99) * mm, "end": v(-450.85, -177.8) * mm});
            skPoint(sketch, "E327.rect.middle", {"position": v(-475.46, -165.9) * mm});
            skLineSegment(sketch, "E328.rect.bottom", {"start": v(-500.06, -206.38) * mm, "end": v(-450.85, -206.38) * mm});
            skLineSegment(sketch, "E328.rect.top", {"start": v(-500.06, -230.19) * mm, "end": v(-450.85, -230.19) * mm});
            skLineSegment(sketch, "E328.rect.left", {"start": v(-500.06, -206.38) * mm, "end": v(-500.06, -230.19) * mm});
            skLineSegment(sketch, "E328.rect.right", {"start": v(-450.85, -206.38) * mm, "end": v(-450.85, -230.19) * mm});
            skPoint(sketch, "E328.rect.middle", {"position": v(-475.46, -218.28) * mm});
            skLineSegment(sketch, "E329.rect.bottom", {"start": v(-427.04, -101.6) * mm, "end": v(-377.82, -101.6) * mm});
            skLineSegment(sketch, "E329.rect.top", {"start": v(-427.04, -125.41) * mm, "end": v(-377.82, -125.41) * mm});
            skLineSegment(sketch, "E329.rect.left", {"start": v(-427.04, -101.6) * mm, "end": v(-427.04, -125.41) * mm});
            skLineSegment(sketch, "E329.rect.right", {"start": v(-377.82, -101.6) * mm, "end": v(-377.82, -125.41) * mm});
            skPoint(sketch, "E329.rect.middle", {"position": v(-402.43, -113.5) * mm});
            skLineSegment(sketch, "E330.rect.bottom", {"start": v(-427.04, -153.99) * mm, "end": v(-377.82, -153.99) * mm});
            skLineSegment(sketch, "E330.rect.top", {"start": v(-427.04, -177.8) * mm, "end": v(-377.82, -177.8) * mm});
            skLineSegment(sketch, "E330.rect.left", {"start": v(-427.04, -153.99) * mm, "end": v(-427.04, -177.8) * mm});
            skLineSegment(sketch, "E330.rect.right", {"start": v(-377.82, -153.99) * mm, "end": v(-377.82, -177.8) * mm});
            skPoint(sketch, "E330.rect.middle", {"position": v(-402.43, -165.9) * mm});
            skLineSegment(sketch, "E331.rect.bottom", {"start": v(-427.04, -206.38) * mm, "end": v(-377.82, -206.38) * mm});
            skLineSegment(sketch, "E331.rect.top", {"start": v(-427.04, -230.19) * mm, "end": v(-377.82, -230.19) * mm});
            skLineSegment(sketch, "E331.rect.left", {"start": v(-427.04, -206.38) * mm, "end": v(-427.04, -230.19) * mm});
            skLineSegment(sketch, "E331.rect.right", {"start": v(-377.82, -206.38) * mm, "end": v(-377.82, -230.19) * mm});
            skPoint(sketch, "E331.rect.middle", {"position": v(-402.43, -218.28) * mm});
            skLineSegment(sketch, "E332.rect.bottom", {"start": v(-354.01, -49.21) * mm, "end": v(-304.8, -49.21) * mm});
            skLineSegment(sketch, "E332.rect.top", {"start": v(-354.01, -73.03) * mm, "end": v(-304.8, -73.03) * mm});
            skLineSegment(sketch, "E332.rect.left", {"start": v(-354.01, -49.21) * mm, "end": v(-354.01, -73.03) * mm});
            skLineSegment(sketch, "E332.rect.right", {"start": v(-304.8, -49.21) * mm, "end": v(-304.8, -73.03) * mm});
            skPoint(sketch, "E332.rect.middle", {"position": v(-329.4, -61.12) * mm});
            skLineSegment(sketch, "E333.rect.bottom", {"start": v(-354.01, -101.6) * mm, "end": v(-304.8, -101.6) * mm});
            skLineSegment(sketch, "E333.rect.top", {"start": v(-354.01, -125.41) * mm, "end": v(-304.8, -125.41) * mm});
            skLineSegment(sketch, "E333.rect.left", {"start": v(-354.01, -101.6) * mm, "end": v(-354.01, -125.41) * mm});
            skLineSegment(sketch, "E333.rect.right", {"start": v(-304.8, -101.6) * mm, "end": v(-304.8, -125.41) * mm});
            skPoint(sketch, "E333.rect.middle", {"position": v(-329.4, -113.5) * mm});
            skLineSegment(sketch, "E334.rect.bottom", {"start": v(-354.01, -153.99) * mm, "end": v(-304.8, -153.99) * mm});
            skLineSegment(sketch, "E334.rect.top", {"start": v(-354.01, -177.8) * mm, "end": v(-304.8, -177.8) * mm});
            skLineSegment(sketch, "E334.rect.left", {"start": v(-354.01, -153.99) * mm, "end": v(-354.01, -177.8) * mm});
            skLineSegment(sketch, "E334.rect.right", {"start": v(-304.8, -153.99) * mm, "end": v(-304.8, -177.8) * mm});
            skPoint(sketch, "E334.rect.middle", {"position": v(-329.4, -165.9) * mm});
            skLineSegment(sketch, "E335.rect.bottom", {"start": v(-354.01, -206.38) * mm, "end": v(-304.8, -206.38) * mm});
            skLineSegment(sketch, "E335.rect.top", {"start": v(-354.01, -230.19) * mm, "end": v(-304.8, -230.19) * mm});
            skLineSegment(sketch, "E335.rect.left", {"start": v(-354.01, -206.38) * mm, "end": v(-354.01, -230.19) * mm});
            skLineSegment(sketch, "E335.rect.right", {"start": v(-304.8, -206.38) * mm, "end": v(-304.8, -230.19) * mm});
            skPoint(sketch, "E335.rect.middle", {"position": v(-329.4, -218.28) * mm});
            skLineSegment(sketch, "E336.rect.bottom", {"start": v(-280.99, -49.21) * mm, "end": v(-231.77, -49.21) * mm});
            skLineSegment(sketch, "E336.rect.top", {"start": v(-280.99, -73.03) * mm, "end": v(-231.77, -73.03) * mm});
            skLineSegment(sketch, "E336.rect.left", {"start": v(-280.99, -49.21) * mm, "end": v(-280.99, -73.03) * mm});
            skLineSegment(sketch, "E336.rect.right", {"start": v(-231.77, -49.21) * mm, "end": v(-231.77, -73.03) * mm});
            skPoint(sketch, "E336.rect.middle", {"position": v(-256.38, -61.12) * mm});
            skLineSegment(sketch, "E337.rect.bottom", {"start": v(-207.96, -49.21) * mm, "end": v(-158.75, -49.21) * mm});
            skLineSegment(sketch, "E337.rect.top", {"start": v(-207.96, -73.03) * mm, "end": v(-158.75, -73.03) * mm});
            skLineSegment(sketch, "E337.rect.left", {"start": v(-207.96, -49.21) * mm, "end": v(-207.96, -73.03) * mm});
            skLineSegment(sketch, "E337.rect.right", {"start": v(-158.75, -49.21) * mm, "end": v(-158.75, -73.03) * mm});
            skPoint(sketch, "E337.rect.middle", {"position": v(-183.36, -61.12) * mm});
            skLineSegment(sketch, "E338.rect.bottom", {"start": v(-134.94, -49.21) * mm, "end": v(-85.72, -49.21) * mm});
            skLineSegment(sketch, "E338.rect.top", {"start": v(-134.94, -73.03) * mm, "end": v(-85.72, -73.03) * mm});
            skLineSegment(sketch, "E338.rect.left", {"start": v(-134.94, -49.21) * mm, "end": v(-134.94, -73.03) * mm});
            skLineSegment(sketch, "E338.rect.right", {"start": v(-85.72, -49.21) * mm, "end": v(-85.72, -73.03) * mm});
            skPoint(sketch, "E338.rect.middle", {"position": v(-110.33, -61.12) * mm});
            skLineSegment(sketch, "E339.rect.bottom", {"start": v(-61.91, -49.21) * mm, "end": v(-12.7, -49.21) * mm});
            skLineSegment(sketch, "E339.rect.top", {"start": v(-61.91, -73.03) * mm, "end": v(-12.7, -73.03) * mm});
            skLineSegment(sketch, "E339.rect.left", {"start": v(-61.91, -49.21) * mm, "end": v(-61.91, -73.03) * mm});
            skLineSegment(sketch, "E339.rect.right", {"start": v(-12.7, -49.21) * mm, "end": v(-12.7, -73.03) * mm});
            skPoint(sketch, "E339.rect.middle", {"position": v(-37.3, -61.12) * mm});
            skLineSegment(sketch, "E340.rect.bottom", {"start": v(11.11, -49.21) * mm, "end": v(60.33, -49.21) * mm});
            skLineSegment(sketch, "E340.rect.top", {"start": v(11.11, -73.03) * mm, "end": v(60.33, -73.03) * mm});
            skLineSegment(sketch, "E340.rect.left", {"start": v(11.11, -49.21) * mm, "end": v(11.11, -73.03) * mm});
            skLineSegment(sketch, "E340.rect.right", {"start": v(60.33, -49.21) * mm, "end": v(60.33, -73.03) * mm});
            skPoint(sketch, "E340.rect.middle", {"position": v(35.72, -61.12) * mm});
            skLineSegment(sketch, "E341.rect.bottom", {"start": v(-280.99, -101.6) * mm, "end": v(-231.77, -101.6) * mm});
            skLineSegment(sketch, "E341.rect.top", {"start": v(-280.99, -125.41) * mm, "end": v(-231.77, -125.41) * mm});
            skLineSegment(sketch, "E341.rect.left", {"start": v(-280.99, -101.6) * mm, "end": v(-280.99, -125.41) * mm});
            skLineSegment(sketch, "E341.rect.right", {"start": v(-231.77, -101.6) * mm, "end": v(-231.77, -125.41) * mm});
            skPoint(sketch, "E341.rect.middle", {"position": v(-256.38, -113.5) * mm});
            skLineSegment(sketch, "E342.rect.bottom", {"start": v(-207.96, -101.6) * mm, "end": v(-158.75, -101.6) * mm});
            skLineSegment(sketch, "E342.rect.top", {"start": v(-207.96, -125.41) * mm, "end": v(-158.75, -125.41) * mm});
            skLineSegment(sketch, "E342.rect.left", {"start": v(-207.96, -101.6) * mm, "end": v(-207.96, -125.41) * mm});
            skLineSegment(sketch, "E342.rect.right", {"start": v(-158.75, -101.6) * mm, "end": v(-158.75, -125.41) * mm});
            skPoint(sketch, "E342.rect.middle", {"position": v(-183.36, -113.5) * mm});
            skLineSegment(sketch, "E343.rect.bottom", {"start": v(-134.94, -101.6) * mm, "end": v(-85.72, -101.6) * mm});
            skLineSegment(sketch, "E343.rect.top", {"start": v(-134.94, -125.41) * mm, "end": v(-85.72, -125.41) * mm});
            skLineSegment(sketch, "E343.rect.left", {"start": v(-134.94, -101.6) * mm, "end": v(-134.94, -125.41) * mm});
            skLineSegment(sketch, "E343.rect.right", {"start": v(-85.72, -101.6) * mm, "end": v(-85.72, -125.41) * mm});
            skPoint(sketch, "E343.rect.middle", {"position": v(-110.33, -113.5) * mm});
            skLineSegment(sketch, "E344.rect.bottom", {"start": v(-61.91, -101.6) * mm, "end": v(-12.7, -101.6) * mm});
            skLineSegment(sketch, "E344.rect.top", {"start": v(-61.91, -125.41) * mm, "end": v(-12.7, -125.41) * mm});
            skLineSegment(sketch, "E344.rect.left", {"start": v(-61.91, -101.6) * mm, "end": v(-61.91, -125.41) * mm});
            skLineSegment(sketch, "E344.rect.right", {"start": v(-12.7, -101.6) * mm, "end": v(-12.7, -125.41) * mm});
            skPoint(sketch, "E344.rect.middle", {"position": v(-37.3, -113.5) * mm});
            skLineSegment(sketch, "E345.rect.bottom", {"start": v(11.11, -101.6) * mm, "end": v(60.33, -101.6) * mm});
            skLineSegment(sketch, "E345.rect.top", {"start": v(11.11, -125.41) * mm, "end": v(60.33, -125.41) * mm});
            skLineSegment(sketch, "E345.rect.left", {"start": v(11.11, -101.6) * mm, "end": v(11.11, -125.41) * mm});
            skLineSegment(sketch, "E345.rect.right", {"start": v(60.33, -101.6) * mm, "end": v(60.33, -125.41) * mm});
            skPoint(sketch, "E345.rect.middle", {"position": v(35.72, -113.5) * mm});
            skLineSegment(sketch, "E346.rect.bottom", {"start": v(-280.99, -153.99) * mm, "end": v(-231.77, -153.99) * mm});
            skLineSegment(sketch, "E346.rect.top", {"start": v(-280.99, -177.8) * mm, "end": v(-231.77, -177.8) * mm});
            skLineSegment(sketch, "E346.rect.left", {"start": v(-280.99, -153.99) * mm, "end": v(-280.99, -177.8) * mm});
            skLineSegment(sketch, "E346.rect.right", {"start": v(-231.77, -153.99) * mm, "end": v(-231.77, -177.8) * mm});
            skPoint(sketch, "E346.rect.middle", {"position": v(-256.38, -165.9) * mm});
            skLineSegment(sketch, "E347.rect.bottom", {"start": v(-207.96, -153.99) * mm, "end": v(-158.75, -153.99) * mm});
            skLineSegment(sketch, "E347.rect.top", {"start": v(-207.96, -177.8) * mm, "end": v(-158.75, -177.8) * mm});
            skLineSegment(sketch, "E347.rect.left", {"start": v(-207.96, -153.99) * mm, "end": v(-207.96, -177.8) * mm});
            skLineSegment(sketch, "E347.rect.right", {"start": v(-158.75, -153.99) * mm, "end": v(-158.75, -177.8) * mm});
            skPoint(sketch, "E347.rect.middle", {"position": v(-183.36, -165.9) * mm});
            skLineSegment(sketch, "E348.rect.bottom", {"start": v(-134.94, -153.99) * mm, "end": v(-85.72, -153.99) * mm});
            skLineSegment(sketch, "E348.rect.top", {"start": v(-134.94, -177.8) * mm, "end": v(-85.72, -177.8) * mm});
            skLineSegment(sketch, "E348.rect.left", {"start": v(-134.94, -153.99) * mm, "end": v(-134.94, -177.8) * mm});
            skLineSegment(sketch, "E348.rect.right", {"start": v(-85.72, -153.99) * mm, "end": v(-85.72, -177.8) * mm});
            skPoint(sketch, "E348.rect.middle", {"position": v(-110.33, -165.9) * mm});
            skLineSegment(sketch, "E349.rect.bottom", {"start": v(-61.91, -153.99) * mm, "end": v(-12.7, -153.99) * mm});
            skLineSegment(sketch, "E349.rect.top", {"start": v(-61.91, -177.8) * mm, "end": v(-12.7, -177.8) * mm});
            skLineSegment(sketch, "E349.rect.left", {"start": v(-61.91, -153.99) * mm, "end": v(-61.91, -177.8) * mm});
            skLineSegment(sketch, "E349.rect.right", {"start": v(-12.7, -153.99) * mm, "end": v(-12.7, -177.8) * mm});
            skPoint(sketch, "E349.rect.middle", {"position": v(-37.3, -165.9) * mm});
            skLineSegment(sketch, "E350.rect.bottom", {"start": v(11.11, -153.99) * mm, "end": v(60.33, -153.99) * mm});
            skLineSegment(sketch, "E350.rect.top", {"start": v(11.11, -177.8) * mm, "end": v(60.33, -177.8) * mm});
            skLineSegment(sketch, "E350.rect.left", {"start": v(11.11, -153.99) * mm, "end": v(11.11, -177.8) * mm});
            skLineSegment(sketch, "E350.rect.right", {"start": v(60.33, -153.99) * mm, "end": v(60.33, -177.8) * mm});
            skPoint(sketch, "E350.rect.middle", {"position": v(35.72, -165.9) * mm});
            skLineSegment(sketch, "E351.rect.bottom", {"start": v(-280.99, -206.38) * mm, "end": v(-231.77, -206.38) * mm});
            skLineSegment(sketch, "E351.rect.top", {"start": v(-280.99, -230.19) * mm, "end": v(-231.77, -230.19) * mm});
            skLineSegment(sketch, "E351.rect.left", {"start": v(-280.99, -206.38) * mm, "end": v(-280.99, -230.19) * mm});
            skLineSegment(sketch, "E351.rect.right", {"start": v(-231.77, -206.38) * mm, "end": v(-231.77, -230.19) * mm});
            skPoint(sketch, "E351.rect.middle", {"position": v(-256.38, -218.28) * mm});
            skLineSegment(sketch, "E352.rect.bottom", {"start": v(-207.96, -206.38) * mm, "end": v(-158.75, -206.38) * mm});
            skLineSegment(sketch, "E352.rect.top", {"start": v(-207.96, -230.19) * mm, "end": v(-158.75, -230.19) * mm});
            skLineSegment(sketch, "E352.rect.left", {"start": v(-207.96, -206.38) * mm, "end": v(-207.96, -230.19) * mm});
            skLineSegment(sketch, "E352.rect.right", {"start": v(-158.75, -206.38) * mm, "end": v(-158.75, -230.19) * mm});
            skPoint(sketch, "E352.rect.middle", {"position": v(-183.36, -218.28) * mm});
            skLineSegment(sketch, "E353.rect.bottom", {"start": v(-134.94, -206.38) * mm, "end": v(-85.72, -206.38) * mm});
            skLineSegment(sketch, "E353.rect.top", {"start": v(-134.94, -230.19) * mm, "end": v(-85.72, -230.19) * mm});
            skLineSegment(sketch, "E353.rect.left", {"start": v(-134.94, -206.38) * mm, "end": v(-134.94, -230.19) * mm});
            skLineSegment(sketch, "E353.rect.right", {"start": v(-85.72, -206.38) * mm, "end": v(-85.72, -230.19) * mm});
            skPoint(sketch, "E353.rect.middle", {"position": v(-110.33, -218.28) * mm});
            skLineSegment(sketch, "E354.rect.bottom", {"start": v(-61.91, -206.38) * mm, "end": v(-12.7, -206.38) * mm});
            skLineSegment(sketch, "E354.rect.top", {"start": v(-61.91, -230.19) * mm, "end": v(-12.7, -230.19) * mm});
            skLineSegment(sketch, "E354.rect.left", {"start": v(-61.91, -206.38) * mm, "end": v(-61.91, -230.19) * mm});
            skLineSegment(sketch, "E354.rect.right", {"start": v(-12.7, -206.38) * mm, "end": v(-12.7, -230.19) * mm});
            skPoint(sketch, "E354.rect.middle", {"position": v(-37.3, -218.28) * mm});
            skLineSegment(sketch, "E355.rect.bottom", {"start": v(11.11, -206.38) * mm, "end": v(60.33, -206.38) * mm});
            skLineSegment(sketch, "E355.rect.top", {"start": v(11.11, -230.19) * mm, "end": v(60.33, -230.19) * mm});
            skLineSegment(sketch, "E355.rect.left", {"start": v(11.11, -206.38) * mm, "end": v(11.11, -230.19) * mm});
            skLineSegment(sketch, "E355.rect.right", {"start": v(60.33, -206.38) * mm, "end": v(60.33, -230.19) * mm});
            skPoint(sketch, "E355.rect.middle", {"position": v(35.72, -218.28) * mm});
            skLineSegment(sketch, "E356", {"start": v(84.14, -61.12) * mm, "end": v(133.35, -61.12) * mm, "construction": true});
            skLineSegment(sketch, "E357", {"start": v(133.35, -61.12) * mm, "end": v(157.16, -61.12) * mm, "construction": true});
            skLineSegment(sketch, "E358", {"start": v(157.16, -61.12) * mm, "end": v(206.38, -61.12) * mm, "construction": true});
            skLineSegment(sketch, "E359", {"start": v(206.38, -61.12) * mm, "end": v(230.19, -61.12) * mm, "construction": true});
            skLineSegment(sketch, "E360", {"start": v(230.19, -61.12) * mm, "end": v(279.4, -61.12) * mm, "construction": true});
            skLineSegment(sketch, "E361", {"start": v(279.4, -61.12) * mm, "end": v(303.21, -61.12) * mm, "construction": true});
            skLineSegment(sketch, "E362", {"start": v(303.21, -61.12) * mm, "end": v(352.43, -61.12) * mm, "construction": true});
            skLineSegment(sketch, "E363", {"start": v(352.43, -61.12) * mm, "end": v(376.24, -61.12) * mm, "construction": true});
            skLineSegment(sketch, "E364", {"start": v(376.24, -61.12) * mm, "end": v(425.45, -61.12) * mm, "construction": true});
            skLineSegment(sketch, "E365", {"start": v(425.45, -61.12) * mm, "end": v(449.26, -61.12) * mm, "construction": true});
            skLineSegment(sketch, "E366", {"start": v(449.26, -61.12) * mm, "end": v(498.48, -61.12) * mm, "construction": true});
            skLineSegment(sketch, "E367", {"start": v(498.48, -61.12) * mm, "end": v(522.29, -61.12) * mm, "construction": true});
            skLineSegment(sketch, "E368", {"start": v(522.29, -61.12) * mm, "end": v(571.5, -61.12) * mm, "construction": true});
            skLineSegment(sketch, "E369", {"start": v(84.14, -113.5) * mm, "end": v(133.35, -113.5) * mm, "construction": true});
            skLineSegment(sketch, "E370", {"start": v(133.35, -113.5) * mm, "end": v(157.16, -113.5) * mm, "construction": true});
            skLineSegment(sketch, "E371", {"start": v(157.16, -113.5) * mm, "end": v(206.38, -113.5) * mm, "construction": true});
            skLineSegment(sketch, "E372", {"start": v(206.38, -113.5) * mm, "end": v(230.19, -113.5) * mm, "construction": true});
            skLineSegment(sketch, "E373", {"start": v(230.19, -113.5) * mm, "end": v(279.4, -113.5) * mm, "construction": true});
            skLineSegment(sketch, "E374", {"start": v(279.4, -113.5) * mm, "end": v(303.21, -113.5) * mm, "construction": true});
            skLineSegment(sketch, "E375", {"start": v(303.21, -113.5) * mm, "end": v(352.43, -113.5) * mm, "construction": true});
            skLineSegment(sketch, "E376", {"start": v(352.43, -113.5) * mm, "end": v(376.24, -113.5) * mm, "construction": true});
            skLineSegment(sketch, "E377", {"start": v(376.24, -113.5) * mm, "end": v(425.45, -113.5) * mm, "construction": true});
            skLineSegment(sketch, "E378", {"start": v(425.45, -113.5) * mm, "end": v(449.26, -113.5) * mm, "construction": true});
            skLineSegment(sketch, "E379", {"start": v(449.26, -113.5) * mm, "end": v(498.48, -113.5) * mm, "construction": true});
            skLineSegment(sketch, "E380", {"start": v(498.48, -113.5) * mm, "end": v(522.29, -113.5) * mm, "construction": true});
            skLineSegment(sketch, "E381", {"start": v(522.29, -113.5) * mm, "end": v(571.5, -113.5) * mm, "construction": true});
            skLineSegment(sketch, "E382", {"start": v(84.14, -165.9) * mm, "end": v(133.35, -165.9) * mm, "construction": true});
            skLineSegment(sketch, "E383", {"start": v(133.35, -165.9) * mm, "end": v(157.16, -165.9) * mm, "construction": true});
            skLineSegment(sketch, "E384", {"start": v(157.16, -165.9) * mm, "end": v(206.38, -165.9) * mm, "construction": true});
            skLineSegment(sketch, "E385", {"start": v(206.38, -165.9) * mm, "end": v(230.19, -165.9) * mm, "construction": true});
            skLineSegment(sketch, "E386", {"start": v(230.19, -165.9) * mm, "end": v(279.4, -165.9) * mm, "construction": true});
            skLineSegment(sketch, "E387", {"start": v(279.4, -165.9) * mm, "end": v(303.21, -165.9) * mm, "construction": true});
            skLineSegment(sketch, "E388", {"start": v(303.21, -165.9) * mm, "end": v(352.43, -165.9) * mm, "construction": true});
            skLineSegment(sketch, "E389", {"start": v(352.43, -165.9) * mm, "end": v(376.24, -165.9) * mm, "construction": true});
            skLineSegment(sketch, "E390", {"start": v(376.24, -165.9) * mm, "end": v(425.45, -165.9) * mm, "construction": true});
            skLineSegment(sketch, "E391", {"start": v(425.45, -165.9) * mm, "end": v(449.26, -165.9) * mm, "construction": true});
            skLineSegment(sketch, "E392", {"start": v(449.26, -165.9) * mm, "end": v(498.48, -165.9) * mm, "construction": true});
            skLineSegment(sketch, "E393", {"start": v(498.48, -165.9) * mm, "end": v(522.29, -165.9) * mm, "construction": true});
            skLineSegment(sketch, "E394", {"start": v(522.29, -165.9) * mm, "end": v(571.5, -165.9) * mm, "construction": true});
            skLineSegment(sketch, "E395", {"start": v(84.14, -218.28) * mm, "end": v(133.35, -218.28) * mm, "construction": true});
            skLineSegment(sketch, "E396", {"start": v(133.35, -218.28) * mm, "end": v(157.16, -218.28) * mm, "construction": true});
            skLineSegment(sketch, "E397", {"start": v(157.16, -218.28) * mm, "end": v(206.38, -218.28) * mm, "construction": true});
            skLineSegment(sketch, "E398", {"start": v(206.38, -218.28) * mm, "end": v(230.19, -218.28) * mm, "construction": true});
            skLineSegment(sketch, "E399", {"start": v(230.19, -218.28) * mm, "end": v(279.4, -218.28) * mm, "construction": true});
            skLineSegment(sketch, "E400", {"start": v(279.4, -218.28) * mm, "end": v(303.21, -218.28) * mm, "construction": true});
            skLineSegment(sketch, "E401", {"start": v(303.21, -218.28) * mm, "end": v(352.43, -218.28) * mm, "construction": true});
            skLineSegment(sketch, "E402", {"start": v(352.43, -218.28) * mm, "end": v(376.24, -218.28) * mm, "construction": true});
            skLineSegment(sketch, "E403", {"start": v(376.24, -218.28) * mm, "end": v(425.45, -218.28) * mm, "construction": true});
            skLineSegment(sketch, "E404", {"start": v(425.45, -218.28) * mm, "end": v(449.26, -218.28) * mm, "construction": true});
            skLineSegment(sketch, "E405", {"start": v(449.26, -218.28) * mm, "end": v(498.48, -218.28) * mm, "construction": true});
            skLineSegment(sketch, "E406", {"start": v(498.48, -218.28) * mm, "end": v(522.29, -218.28) * mm, "construction": true});
            skLineSegment(sketch, "E407", {"start": v(522.29, -218.28) * mm, "end": v(571.5, -218.28) * mm, "construction": true});
            skLineSegment(sketch, "E408.rect.bottom", {"start": v(84.14, -49.21) * mm, "end": v(133.35, -49.21) * mm});
            skLineSegment(sketch, "E408.rect.top", {"start": v(84.14, -73.03) * mm, "end": v(133.35, -73.03) * mm});
            skLineSegment(sketch, "E408.rect.left", {"start": v(84.14, -49.21) * mm, "end": v(84.14, -73.03) * mm});
            skLineSegment(sketch, "E408.rect.right", {"start": v(133.35, -49.21) * mm, "end": v(133.35, -73.03) * mm});
            skPoint(sketch, "E408.rect.middle", {"position": v(108.74, -61.12) * mm});
            skLineSegment(sketch, "E409.rect.bottom", {"start": v(84.14, -101.6) * mm, "end": v(133.35, -101.6) * mm});
            skLineSegment(sketch, "E409.rect.top", {"start": v(84.14, -125.41) * mm, "end": v(133.35, -125.41) * mm});
            skLineSegment(sketch, "E409.rect.left", {"start": v(84.14, -101.6) * mm, "end": v(84.14, -125.41) * mm});
            skLineSegment(sketch, "E409.rect.right", {"start": v(133.35, -101.6) * mm, "end": v(133.35, -125.41) * mm});
            skPoint(sketch, "E409.rect.middle", {"position": v(108.74, -113.5) * mm});
            skLineSegment(sketch, "E410.rect.bottom", {"start": v(84.14, -153.99) * mm, "end": v(133.35, -153.99) * mm});
            skLineSegment(sketch, "E410.rect.top", {"start": v(84.14, -177.8) * mm, "end": v(133.35, -177.8) * mm});
            skLineSegment(sketch, "E410.rect.left", {"start": v(84.14, -153.99) * mm, "end": v(84.14, -177.8) * mm});
            skLineSegment(sketch, "E410.rect.right", {"start": v(133.35, -153.99) * mm, "end": v(133.35, -177.8) * mm});
            skPoint(sketch, "E410.rect.middle", {"position": v(108.74, -165.9) * mm});
            skLineSegment(sketch, "E411.rect.bottom", {"start": v(84.14, -206.38) * mm, "end": v(133.35, -206.38) * mm});
            skLineSegment(sketch, "E411.rect.top", {"start": v(84.14, -230.19) * mm, "end": v(133.35, -230.19) * mm});
            skLineSegment(sketch, "E411.rect.left", {"start": v(84.14, -206.38) * mm, "end": v(84.14, -230.19) * mm});
            skLineSegment(sketch, "E411.rect.right", {"start": v(133.35, -206.38) * mm, "end": v(133.35, -230.19) * mm});
            skPoint(sketch, "E411.rect.middle", {"position": v(108.74, -218.28) * mm});
            skLineSegment(sketch, "E412.rect.bottom", {"start": v(157.16, -49.21) * mm, "end": v(206.38, -49.21) * mm});
            skLineSegment(sketch, "E412.rect.top", {"start": v(157.16, -73.03) * mm, "end": v(206.38, -73.03) * mm});
            skLineSegment(sketch, "E412.rect.left", {"start": v(157.16, -49.21) * mm, "end": v(157.16, -73.03) * mm});
            skLineSegment(sketch, "E412.rect.right", {"start": v(206.38, -49.21) * mm, "end": v(206.38, -73.03) * mm});
            skPoint(sketch, "E412.rect.middle", {"position": v(181.77, -61.12) * mm});
            skLineSegment(sketch, "E413.rect.bottom", {"start": v(157.16, -101.6) * mm, "end": v(206.38, -101.6) * mm});
            skLineSegment(sketch, "E413.rect.top", {"start": v(157.16, -125.41) * mm, "end": v(206.38, -125.41) * mm});
            skLineSegment(sketch, "E413.rect.left", {"start": v(157.16, -101.6) * mm, "end": v(157.16, -125.41) * mm});
            skLineSegment(sketch, "E413.rect.right", {"start": v(206.38, -101.6) * mm, "end": v(206.38, -125.41) * mm});
            skPoint(sketch, "E413.rect.middle", {"position": v(181.77, -113.5) * mm});
            skLineSegment(sketch, "E414.rect.bottom", {"start": v(157.16, -153.99) * mm, "end": v(206.38, -153.99) * mm});
            skLineSegment(sketch, "E414.rect.top", {"start": v(157.16, -177.8) * mm, "end": v(206.38, -177.8) * mm});
            skLineSegment(sketch, "E414.rect.left", {"start": v(157.16, -153.99) * mm, "end": v(157.16, -177.8) * mm});
            skLineSegment(sketch, "E414.rect.right", {"start": v(206.38, -153.99) * mm, "end": v(206.38, -177.8) * mm});
            skPoint(sketch, "E414.rect.middle", {"position": v(181.77, -165.9) * mm});
            skLineSegment(sketch, "E415.rect.bottom", {"start": v(157.16, -206.38) * mm, "end": v(206.38, -206.38) * mm});
            skLineSegment(sketch, "E415.rect.top", {"start": v(157.16, -230.19) * mm, "end": v(206.38, -230.19) * mm});
            skLineSegment(sketch, "E415.rect.left", {"start": v(157.16, -206.38) * mm, "end": v(157.16, -230.19) * mm});
            skLineSegment(sketch, "E415.rect.right", {"start": v(206.38, -206.38) * mm, "end": v(206.38, -230.19) * mm});
            skPoint(sketch, "E415.rect.middle", {"position": v(181.77, -218.28) * mm});
            skLineSegment(sketch, "E416.rect.bottom", {"start": v(230.19, -49.21) * mm, "end": v(279.4, -49.21) * mm});
            skLineSegment(sketch, "E416.rect.top", {"start": v(230.19, -73.03) * mm, "end": v(279.4, -73.03) * mm});
            skLineSegment(sketch, "E416.rect.left", {"start": v(230.19, -49.21) * mm, "end": v(230.19, -73.03) * mm});
            skLineSegment(sketch, "E416.rect.right", {"start": v(279.4, -49.21) * mm, "end": v(279.4, -73.03) * mm});
            skPoint(sketch, "E416.rect.middle", {"position": v(254.8, -61.12) * mm});
            skLineSegment(sketch, "E417.rect.bottom", {"start": v(230.19, -101.6) * mm, "end": v(279.4, -101.6) * mm});
            skLineSegment(sketch, "E417.rect.top", {"start": v(230.19, -125.41) * mm, "end": v(279.4, -125.41) * mm});
            skLineSegment(sketch, "E417.rect.left", {"start": v(230.19, -101.6) * mm, "end": v(230.19, -125.41) * mm});
            skLineSegment(sketch, "E417.rect.right", {"start": v(279.4, -101.6) * mm, "end": v(279.4, -125.41) * mm});
            skPoint(sketch, "E417.rect.middle", {"position": v(254.8, -113.5) * mm});
            skLineSegment(sketch, "E418.rect.bottom", {"start": v(230.19, -153.99) * mm, "end": v(279.4, -153.99) * mm});
            skLineSegment(sketch, "E418.rect.top", {"start": v(230.19, -177.8) * mm, "end": v(279.4, -177.8) * mm});
            skLineSegment(sketch, "E418.rect.left", {"start": v(230.19, -153.99) * mm, "end": v(230.19, -177.8) * mm});
            skLineSegment(sketch, "E418.rect.right", {"start": v(279.4, -153.99) * mm, "end": v(279.4, -177.8) * mm});
            skPoint(sketch, "E418.rect.middle", {"position": v(254.8, -165.9) * mm});
            skLineSegment(sketch, "E419.rect.bottom", {"start": v(230.19, -206.38) * mm, "end": v(279.4, -206.38) * mm});
            skLineSegment(sketch, "E419.rect.top", {"start": v(230.19, -230.19) * mm, "end": v(279.4, -230.19) * mm});
            skLineSegment(sketch, "E419.rect.left", {"start": v(230.19, -206.38) * mm, "end": v(230.19, -230.19) * mm});
            skLineSegment(sketch, "E419.rect.right", {"start": v(279.4, -206.38) * mm, "end": v(279.4, -230.19) * mm});
            skPoint(sketch, "E419.rect.middle", {"position": v(254.8, -218.28) * mm});
            skLineSegment(sketch, "E420.rect.bottom", {"start": v(303.21, -49.21) * mm, "end": v(352.43, -49.21) * mm});
            skLineSegment(sketch, "E420.rect.top", {"start": v(303.21, -73.03) * mm, "end": v(352.43, -73.03) * mm});
            skLineSegment(sketch, "E420.rect.left", {"start": v(303.21, -49.21) * mm, "end": v(303.21, -73.03) * mm});
            skLineSegment(sketch, "E420.rect.right", {"start": v(352.43, -49.21) * mm, "end": v(352.43, -73.03) * mm});
            skPoint(sketch, "E420.rect.middle", {"position": v(327.82, -61.12) * mm});
            skLineSegment(sketch, "E421.rect.bottom", {"start": v(303.21, -101.6) * mm, "end": v(352.43, -101.6) * mm});
            skLineSegment(sketch, "E421.rect.top", {"start": v(303.21, -125.41) * mm, "end": v(352.43, -125.41) * mm});
            skLineSegment(sketch, "E421.rect.left", {"start": v(303.21, -101.6) * mm, "end": v(303.21, -125.41) * mm});
            skLineSegment(sketch, "E421.rect.right", {"start": v(352.43, -101.6) * mm, "end": v(352.43, -125.41) * mm});
            skPoint(sketch, "E421.rect.middle", {"position": v(327.82, -113.5) * mm});
            skLineSegment(sketch, "E422.rect.bottom", {"start": v(303.21, -153.99) * mm, "end": v(352.43, -153.99) * mm});
            skLineSegment(sketch, "E422.rect.top", {"start": v(303.21, -177.8) * mm, "end": v(352.43, -177.8) * mm});
            skLineSegment(sketch, "E422.rect.left", {"start": v(303.21, -153.99) * mm, "end": v(303.21, -177.8) * mm});
            skLineSegment(sketch, "E422.rect.right", {"start": v(352.43, -153.99) * mm, "end": v(352.43, -177.8) * mm});
            skPoint(sketch, "E422.rect.middle", {"position": v(327.82, -165.9) * mm});
            skLineSegment(sketch, "E423.rect.bottom", {"start": v(303.21, -206.38) * mm, "end": v(352.43, -206.38) * mm});
            skLineSegment(sketch, "E423.rect.top", {"start": v(303.21, -230.19) * mm, "end": v(352.43, -230.19) * mm});
            skLineSegment(sketch, "E423.rect.left", {"start": v(303.21, -206.38) * mm, "end": v(303.21, -230.19) * mm});
            skLineSegment(sketch, "E423.rect.right", {"start": v(352.43, -206.38) * mm, "end": v(352.43, -230.19) * mm});
            skPoint(sketch, "E423.rect.middle", {"position": v(327.82, -218.28) * mm});
            skLineSegment(sketch, "E424.rect.bottom", {"start": v(376.24, -49.21) * mm, "end": v(425.45, -49.21) * mm});
            skLineSegment(sketch, "E424.rect.top", {"start": v(376.24, -73.03) * mm, "end": v(425.45, -73.03) * mm});
            skLineSegment(sketch, "E424.rect.left", {"start": v(376.24, -49.21) * mm, "end": v(376.24, -73.03) * mm});
            skLineSegment(sketch, "E424.rect.right", {"start": v(425.45, -49.21) * mm, "end": v(425.45, -73.03) * mm});
            skPoint(sketch, "E424.rect.middle", {"position": v(400.84, -61.12) * mm});
            skLineSegment(sketch, "E425.rect.bottom", {"start": v(376.24, -101.6) * mm, "end": v(425.45, -101.6) * mm});
            skLineSegment(sketch, "E425.rect.top", {"start": v(376.24, -125.41) * mm, "end": v(425.45, -125.41) * mm});
            skLineSegment(sketch, "E425.rect.left", {"start": v(376.24, -101.6) * mm, "end": v(376.24, -125.41) * mm});
            skLineSegment(sketch, "E425.rect.right", {"start": v(425.45, -101.6) * mm, "end": v(425.45, -125.41) * mm});
            skPoint(sketch, "E425.rect.middle", {"position": v(400.84, -113.5) * mm});
            skLineSegment(sketch, "E426.rect.bottom", {"start": v(376.24, -153.99) * mm, "end": v(425.45, -153.99) * mm});
            skLineSegment(sketch, "E426.rect.top", {"start": v(376.24, -177.8) * mm, "end": v(425.45, -177.8) * mm});
            skLineSegment(sketch, "E426.rect.left", {"start": v(376.24, -153.99) * mm, "end": v(376.24, -177.8) * mm});
            skLineSegment(sketch, "E426.rect.right", {"start": v(425.45, -153.99) * mm, "end": v(425.45, -177.8) * mm});
            skPoint(sketch, "E426.rect.middle", {"position": v(400.84, -165.9) * mm});
            skLineSegment(sketch, "E427.rect.bottom", {"start": v(376.24, -206.38) * mm, "end": v(425.45, -206.38) * mm});
            skLineSegment(sketch, "E427.rect.top", {"start": v(376.24, -230.19) * mm, "end": v(425.45, -230.19) * mm});
            skLineSegment(sketch, "E427.rect.left", {"start": v(376.24, -206.38) * mm, "end": v(376.24, -230.19) * mm});
            skLineSegment(sketch, "E427.rect.right", {"start": v(425.45, -206.38) * mm, "end": v(425.45, -230.19) * mm});
            skPoint(sketch, "E427.rect.middle", {"position": v(400.84, -218.28) * mm});
            skLineSegment(sketch, "E428.rect.bottom", {"start": v(449.26, -49.21) * mm, "end": v(498.48, -49.21) * mm});
            skLineSegment(sketch, "E428.rect.top", {"start": v(449.26, -73.03) * mm, "end": v(498.48, -73.03) * mm});
            skLineSegment(sketch, "E428.rect.left", {"start": v(449.26, -49.21) * mm, "end": v(449.26, -73.03) * mm});
            skLineSegment(sketch, "E428.rect.right", {"start": v(498.48, -49.21) * mm, "end": v(498.48, -73.03) * mm});
            skPoint(sketch, "E428.rect.middle", {"position": v(473.87, -61.12) * mm});
            skLineSegment(sketch, "E429.rect.bottom", {"start": v(449.26, -101.6) * mm, "end": v(498.48, -101.6) * mm});
            skLineSegment(sketch, "E429.rect.top", {"start": v(449.26, -125.41) * mm, "end": v(498.48, -125.41) * mm});
            skLineSegment(sketch, "E429.rect.left", {"start": v(449.26, -101.6) * mm, "end": v(449.26, -125.41) * mm});
            skLineSegment(sketch, "E429.rect.right", {"start": v(498.48, -101.6) * mm, "end": v(498.48, -125.41) * mm});
            skPoint(sketch, "E429.rect.middle", {"position": v(473.87, -113.5) * mm});
            skLineSegment(sketch, "E430.rect.bottom", {"start": v(449.26, -153.99) * mm, "end": v(498.48, -153.99) * mm});
            skLineSegment(sketch, "E430.rect.top", {"start": v(449.26, -177.8) * mm, "end": v(498.48, -177.8) * mm});
            skLineSegment(sketch, "E430.rect.left", {"start": v(449.26, -153.99) * mm, "end": v(449.26, -177.8) * mm});
            skLineSegment(sketch, "E430.rect.right", {"start": v(498.48, -153.99) * mm, "end": v(498.48, -177.8) * mm});
            skPoint(sketch, "E430.rect.middle", {"position": v(473.87, -165.9) * mm});
            skLineSegment(sketch, "E431.rect.bottom", {"start": v(449.26, -206.38) * mm, "end": v(498.48, -206.38) * mm});
            skLineSegment(sketch, "E431.rect.top", {"start": v(449.26, -230.19) * mm, "end": v(498.48, -230.19) * mm});
            skLineSegment(sketch, "E431.rect.left", {"start": v(449.26, -206.38) * mm, "end": v(449.26, -230.19) * mm});
            skLineSegment(sketch, "E431.rect.right", {"start": v(498.48, -206.38) * mm, "end": v(498.48, -230.19) * mm});
            skPoint(sketch, "E431.rect.middle", {"position": v(473.87, -218.28) * mm});
            skLineSegment(sketch, "E432.rect.bottom", {"start": v(522.29, -49.21) * mm, "end": v(571.5, -49.21) * mm});
            skLineSegment(sketch, "E432.rect.top", {"start": v(522.29, -73.03) * mm, "end": v(571.5, -73.03) * mm});
            skLineSegment(sketch, "E432.rect.left", {"start": v(522.29, -49.21) * mm, "end": v(522.29, -73.03) * mm});
            skLineSegment(sketch, "E432.rect.right", {"start": v(571.5, -49.21) * mm, "end": v(571.5, -73.03) * mm});
            skPoint(sketch, "E432.rect.middle", {"position": v(546.9, -61.12) * mm});
            skLineSegment(sketch, "E433.rect.bottom", {"start": v(522.29, -101.6) * mm, "end": v(571.5, -101.6) * mm});
            skLineSegment(sketch, "E433.rect.top", {"start": v(522.29, -125.41) * mm, "end": v(571.5, -125.41) * mm});
            skLineSegment(sketch, "E433.rect.left", {"start": v(522.29, -101.6) * mm, "end": v(522.29, -125.41) * mm});
            skLineSegment(sketch, "E433.rect.right", {"start": v(571.5, -101.6) * mm, "end": v(571.5, -125.41) * mm});
            skPoint(sketch, "E433.rect.middle", {"position": v(546.9, -113.5) * mm});
            skLineSegment(sketch, "E434.rect.bottom", {"start": v(522.29, -153.99) * mm, "end": v(571.5, -153.99) * mm});
            skLineSegment(sketch, "E434.rect.top", {"start": v(522.29, -177.8) * mm, "end": v(571.5, -177.8) * mm});
            skLineSegment(sketch, "E434.rect.left", {"start": v(522.29, -153.99) * mm, "end": v(522.29, -177.8) * mm});
            skLineSegment(sketch, "E434.rect.right", {"start": v(571.5, -153.99) * mm, "end": v(571.5, -177.8) * mm});
            skPoint(sketch, "E434.rect.middle", {"position": v(546.9, -165.9) * mm});
            skLineSegment(sketch, "E435.rect.bottom", {"start": v(522.29, -206.38) * mm, "end": v(571.5, -206.38) * mm});
            skLineSegment(sketch, "E435.rect.top", {"start": v(522.29, -230.19) * mm, "end": v(571.5, -230.19) * mm});
            skLineSegment(sketch, "E435.rect.left", {"start": v(522.29, -206.38) * mm, "end": v(522.29, -230.19) * mm});
            skLineSegment(sketch, "E435.rect.right", {"start": v(571.5, -206.38) * mm, "end": v(571.5, -230.19) * mm});
            skPoint(sketch, "E435.rect.middle", {"position": v(546.9, -218.28) * mm});
            skSolve(sketch);
        }
        {
            var Q0;
            Q0 = qSketchRegion(id + "F6", true);
            extrude(context, id + "F7", {"entities" : qUnion([Q0]), "operationType" : NewBodyOperationType.ADD, "depth" : 6.35 * mm});
        }
    });
